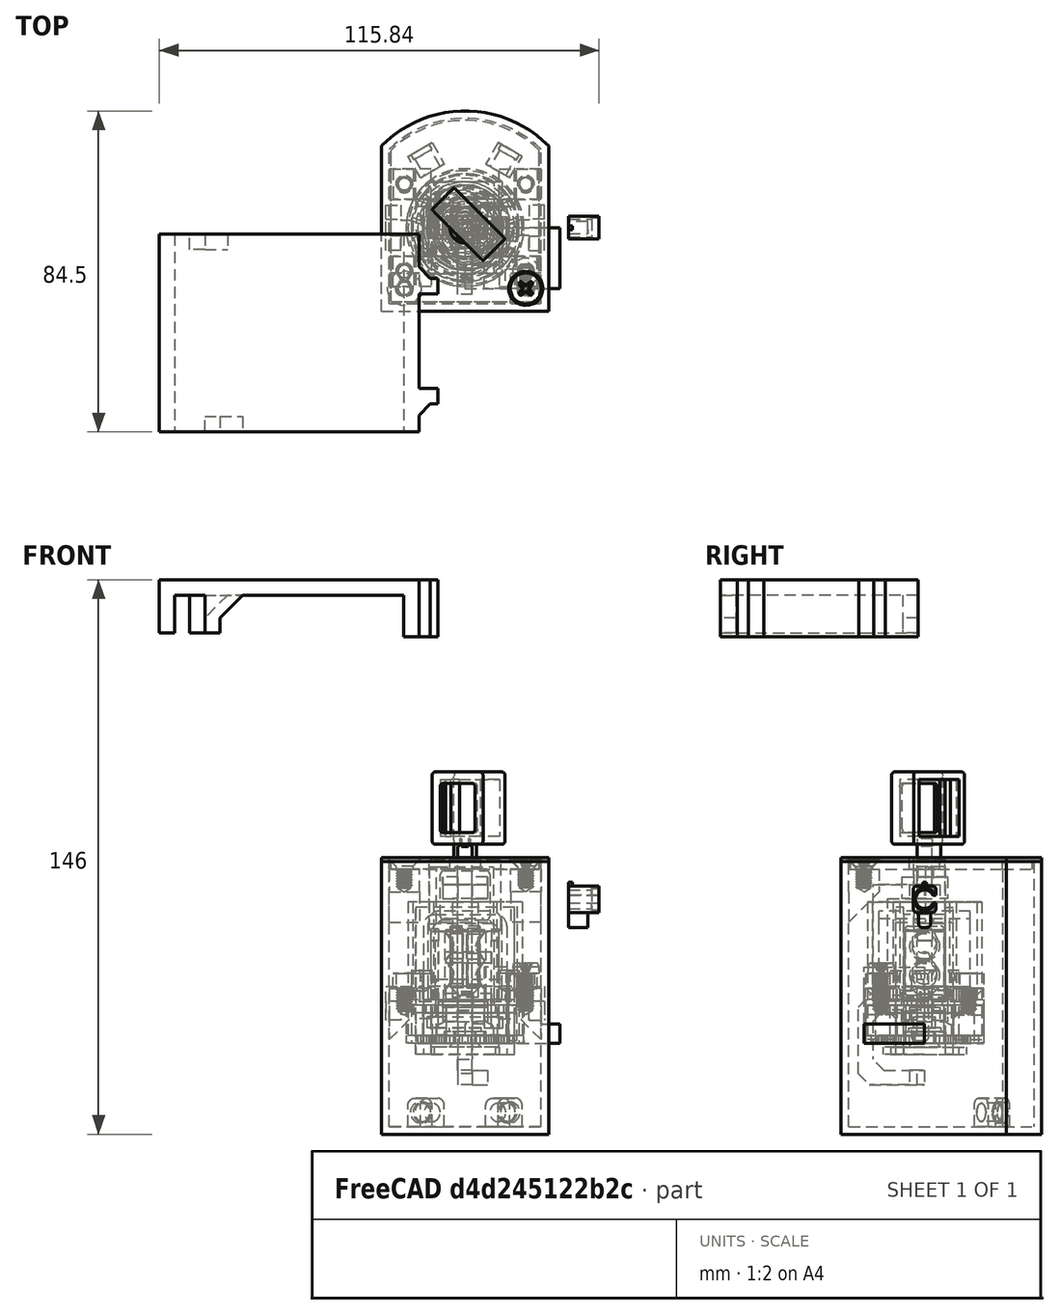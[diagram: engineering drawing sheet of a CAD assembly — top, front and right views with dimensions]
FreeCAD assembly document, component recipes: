
FREECAD ASSEMBLY — COMPONENT RECIPES ("laser2-1mm")

This assembly document has 31 components, labeled P0..P30 below (a component is one placed body or linked part). 31 of them carry a construction recipe — the FreeCAD feature program that regenerates the part from scratch, quoted from this document or its linked companion documents; the rest are supplied as boundary geometry only. No exploded tour is included for this assembly.
NOTE — this tour is split across 2 documents so each fits a 32k-token context. This is document 1: the component sections continue in the remaining 1 document, each repeating the header above.
COMPONENT P0 — recipe-attached ("stator", modeled in this document).
Construction recipe (the document's own serialized feature program — sketch geometry with constraints, then the solid features built on it; lengths are millimeters unless a unit is written):

FEATURE [PartDesign::SubShapeBinder] Binder
  BindCopyOnChange = 0
  BindMode = 0
  ClaimChildren = false
  Context = -> Body [Binder.]
  Fuse = false
  MakeFace = true
  OffsetFill = false
  OffsetIntersection = false
  OffsetJoinType = 0
  OffsetOpenResult = false
  PartialLoad = false
  Refine = true
  Relative = true
  Support = -> [Body020]
  _Version = 2
FEATURE [Sketcher::SketchObject] Sketch100
  ArcFitTolerance = 1e-06
  AttachmentSupport = -> [Origin]
  ExternalGeometry = -> [Binder]
  ExternalTypes = [0,0]
  FullyConstrained = false
  MakeInternals = false
  MapMode = 5
  sketch-geometry (3):
    g0: Circle CenterX=0 CenterY=0 CenterZ=0 NormalX=0 NormalY=0 NormalZ=1 AngleXU=0 Radius=11.2
    g1: GeomPoint [constr] X=-5.17153 Y=14.2087 Z=0
    g2: Circle CenterX=0 CenterY=0 CenterZ=0 NormalX=0 NormalY=0 NormalZ=1 AngleXU=0 Radius=14.2
  constraints (4):
    c: Coincident(g0,g-4)
    c: Distance(g-4,g0) = 0.2
    c: Coincident(g2,g0)
    c: Distance(g2,g0) = 3
FEATURE [PartDesign::Pad] Pad
  Direction = (0,0,1)
  Length = 10
  Length2 = 10
  Profile = -> Sketch100
  ReferenceAxis = -> Sketch100 [N_Axis]
  Refine = true
  SideType = 0
  Suppressed = false
  Type = 3
  Type2 = 0
  UpToFace = -> Binder [Face1]
FEATURE [PartDesign::SubShapeBinder] Binder024
  BindCopyOnChange = 0
  BindMode = 0
  ClaimChildren = false
  Context = -> Body [Binder024.]
  Fuse = false
  MakeFace = true
  OffsetFill = false
  OffsetIntersection = false
  OffsetJoinType = 0
  OffsetOpenResult = false
  PartialLoad = false
  Refine = true
  Relative = true
  Support = -> [Body022]
  _Version = 2
FEATURE [Sketcher::SketchObject] Sketch102
  ArcFitTolerance = 1e-06
  AttachmentSupport = -> [Binder024]
  ExternalGeometry = -> [Binder024]
  ExternalTypes = [0,0]
  FullyConstrained = true
  MakeInternals = false
  MapMode = 5
  Placement = pos=(-7,0,0) rot=(0.57735,0.57735,0.57735;2.0944rad)
  sketch-geometry (2):
    g0: LineSegment [constr] StartX=0 StartY=13 StartZ=0 EndX=0 EndY=21 EndZ=0
    g1: GeomPoint X=0 Y=17 Z=0
  constraints (5):
    c: PointOnObject(g0,g-4)
    c: PointOnObject(g0,g-3)
    c: Vertical(g0)
    c: PointOnObject(g0,g-2)
    c: Symmetric(g0,g0,g1)
FEATURE [Part::DatumPlane] DatumPlane003
  AttachmentSupport = -> [Sketch102]
  MapMode = 1
  Placement = pos=(-7,0,17) rot=(0,0,1;0rad)
FEATURE [Sketcher::SketchObject] Sketch104
  ArcFitTolerance = 1e-06
  AttachmentSupport = -> [Pad]
  ExternalGeometry = -> [Pad]
  ExternalTypes = [0,0]
  FullyConstrained = true
  MakeInternals = false
  MapMode = 5
  Placement = pos=(0,0,2) rot=(0,0,1;0rad)
  expr: Constraints[9] = VarSet.target_angle * 2
  sketch-geometry (6):
    g0: ArcOfCircle CenterX=0 CenterY=0 CenterZ=0 NormalX=0 NormalY=0 NormalZ=1 AngleXU=0 Radius=14.2 StartAngle=0 EndAngle=0.698132
    g1: GeomPoint X=14.2 Y=0 Z=0
    g2: LineSegment StartX=10.8778 StartY=9.12758 StartZ=0 EndX=8.5797 EndY=7.19922 EndZ=0
    g3: LineSegment StartX=14.2 StartY=0 StartZ=0 EndX=11.2 EndY=0 EndZ=0
    g4: ArcOfCircle CenterX=0 CenterY=0 CenterZ=0 NormalX=0 NormalY=0 NormalZ=1 AngleXU=0 Radius=11.2 StartAngle=0 EndAngle=0.698132
    g5: LineSegment [constr] StartX=0 StartY=0 StartZ=0 EndX=10.8778 EndY=9.12758 EndZ=0
  constraints (15):
    c: Coincident(g0,g-1)
    c: PointOnObject(g1,g-1)
    c: Coincident(g0,g1)
    c: Coincident(g3,g0)
    c: PointOnObject(g3,g-1)
    c: Coincident(g3,g4)
    c: Coincident(g4,g2)
    c: Coincident(g4,g-1)
    c: Coincident(g5,g-1)
    c: Angle(g-1,g5) = 0.698132
    c: PointOnObject(g5,g-3)
    c: Coincident(g0,g5)
    c: Coincident(g2,g0)
    c: PointOnObject(g2,g5)
    c: PointOnObject(g2,g-4)
FEATURE [PartDesign::Pad] Pad065
  BaseFeature = -> Pad
  Direction = (0,0,1)
  Length = 10
  Length2 = 10
  Offset = 2.13333
  Profile = -> Sketch104
  ReferenceAxis = -> Sketch104 [N_Axis]
  Refine = true
  SideType = 0
  Suppressed = false
  Type = 3
  Type2 = 0
  UpToFace = -> DatumPlane003
  expr: Offset = 2 / 3 * VarSet.magnet_diameter / 2
FEATURE [Sketcher::SketchObject] Sketch105
  ArcFitTolerance = 1e-06
  AttachmentSupport = -> [Pad065]
  ExternalGeometry = -> [Pad065]
  ExternalTypes = [0]
  FullyConstrained = false
  MakeInternals = false
  MapMode = 5
  Placement = pos=(0,0,19.1333) rot=(0,0,1;0rad)
  sketch-geometry (2):
    g0: LineSegment StartX=0 StartY=0 StartZ=0 EndX=10.4708 EndY=3.97514 EndZ=0
    g1: GeomPoint X=10.4708 Y=3.97514 Z=0
  constraints (3):
    c: Coincident(g0,g-5)
    c: PointOnObject(g0,g-5)
    c: Coincident(g0,g1)
FEATURE [Part::DatumPlane] DatumPlane004
  AttachmentOffset = pos=(0,0,2) rot=(0,0,1;0rad)
  AttachmentSupport = -> [Sketch105]
  MapMode = 7
  Placement = pos=(8.60104,3.26529,19.1333) rot=(0.715712,-0.49384,-0.49384;1.89921rad)
FEATURE [Sketcher::SketchObject] Sketch106
  ArcFitTolerance = 1e-06
  AttachmentSupport = -> [DatumPlane004]
  ExternalGeometry = -> [Binder024]
  ExternalTypes = [0,0]
  FullyConstrained = true
  MakeInternals = false
  MapMode = 5
  Placement = pos=(8.60104,3.26529,19.1333) rot=(0.715712,-0.49384,-0.49384;1.89921rad)
  expr: Constraints[11] = VarSet.magnet_diameter
  sketch-geometry (5):
    g0: LineSegment [constr] StartX=2.48446 StartY=-7.63333 StartZ=0 EndX=2.48446 EndY=-6.13333 EndZ=0
    g1: LineSegment [constr] StartX=2.48446 StartY=-6.13333 StartZ=0 EndX=2.48446 EndY=1.86667 EndZ=0
    g2: GeomPoint [constr] X=2.48446 Y=-2.13333 Z=0
    g3: LineSegment [constr] StartX=2.48446 StartY=-2.13333 StartZ=0 EndX=0 EndY=-2.13333 EndZ=0
    g4: Circle CenterX=0 CenterY=-2.13333 CenterZ=0 NormalX=0 NormalY=0 NormalZ=1 AngleXU=0 Radius=3.2
  constraints (12):
    c: Coincident(g0,g-4)
    c: PointOnObject(g0,g-4)
    c: Vertical(g0)
    c: Coincident(g1,g0)
    c: PointOnObject(g1,g-3)
    c: Vertical(g1)
    c: Symmetric(g1,g1,g2)
    c: Coincident(g3,g2)
    c: PointOnObject(g3,g-2)
    c: Horizontal(g3)
    c: Coincident(g4,g3)
    c: Diameter(g4) = 6.4
FEATURE [PartDesign::Pocket] Pocket024
  BaseFeature = -> Pad065
  Direction = (0.934895,0.354923,-1e-16)
  Length = 5.2
  Length2 = 5
  Profile = -> Sketch106
  ReferenceAxis = -> Sketch106 [N_Axis]
  Refine = true
  SideType = 0
  Suppressed = false
  Type = 0
  Type2 = 0
  expr: Length = 2 mm + VarSet.magnet_height
FEATURE [PartDesign::Mirrored] Mirror
  MirrorPlane = -> XZ_Plane
  Refine = true
  Suppressed = false
  TransformMode = 0
FEATURE [PartDesign::Mirrored] Mirror008
  MirrorPlane = -> YZ_Plane
  Refine = true
  Suppressed = false
  TransformMode = 0
FEATURE [PartDesign::MultiTransform] MultiTransform
  BaseFeature = -> Pocket024
  Originals = -> [Pad065,Pad,Pocket024]
  Refine = true
  Suppressed = false
  TransformMode = 0
  Transformations = -> [Mirror,Mirror008]
FEATURE [PartDesign::Body] Body  label="stator"
  AllowCompound = false
  Group = -> [Sketch100,Binder,Pad,Binder024,Sketch102,DatumPlane003,Sketch104,Pad065,Sketch105,DatumPlane004,Sketch106,Pocket024,MultiTransform,Mirror,Mirror008]
  Origin = -> Origin
  Tip = -> MultiTransform
COMPONENT P1 — recipe-attached ("bearing", modeled in this document).
Construction recipe (the document's own serialized feature program — sketch geometry with constraints, then the solid features built on it; lengths are millimeters unless a unit is written):

FEATURE [Sketcher::SketchObject] Sketch002
  ArcFitTolerance = 1e-06
  AttachmentSupport = -> [Origin004]
  ExternalTypes = [0]
  FullyConstrained = true
  MakeInternals = false
  MapMode = 5
  expr: Constraints[1] = VarSet.bearing_inner_diameter
  expr: Constraints[3] = VarSet.bearing_diameter
  sketch-geometry (2):
    g0: Circle CenterX=0 CenterY=0 CenterZ=0 NormalX=0 NormalY=0 NormalZ=1 AngleXU=0 Radius=5
    g1: Circle CenterX=0 CenterY=0 CenterZ=0 NormalX=0 NormalY=0 NormalZ=1 AngleXU=0 Radius=13
  constraints (4):
    c: Coincident(g0,g-1)
    c: Diameter(g0) = 10
    c: Coincident(g1,g0)
    c: Diameter(g1) = 26
FEATURE [PartDesign::Pad] Pad001
  Direction = (0,0,1)
  Length = 8
  Length2 = 10
  Profile = -> Sketch002
  ReferenceAxis = -> Sketch002 [N_Axis]
  Refine = true
  SideType = 0
  Suppressed = false
  Type = 0
  Type2 = 0
  expr: Length = VarSet.bearing_height
FEATURE [PartDesign::Body] Body002  label="bearing"
  AllowCompound = false
  Group = -> [Sketch002,Pad001]
  Origin = -> Origin004
  Tip = -> Pad001
COMPONENT P2 — recipe-attached ("mirror_holder_adapter", modeled in this document).
Construction recipe (the document's own serialized feature program — sketch geometry with constraints, then the solid features built on it; lengths are millimeters unless a unit is written):

FEATURE [PartDesign::SubShapeBinder] Binder005
  BindCopyOnChange = 0
  BindMode = 0
  ClaimChildren = false
  Context = -> Body004 [Binder005.]
  Fuse = false
  MakeFace = true
  OffsetFill = false
  OffsetIntersection = false
  OffsetJoinType = 0
  OffsetOpenResult = false
  PartialLoad = false
  Refine = true
  Relative = true
  _Version = 2
FEATURE [Sketcher::SketchObject] Sketch028
  ArcFitTolerance = 1e-06
  AttachmentSupport = -> [Binder005]
  ExternalGeometry = -> [Binder005]
  ExternalTypes = [0,0,0,0,0,0,0]
  FullyConstrained = false
  MakeInternals = false
  MapMode = 5
  Placement = pos=(0,0,11) rot=(0,0,1;0rad)
  sketch-geometry (13):
    g0: LineSegment StartX=20.8819 StartY=-6 StartZ=0 EndX=20.8819 EndY=6 EndZ=0
    g1: LineSegment StartX=20.8819 StartY=6 StartZ=0 EndX=16.8819 EndY=6 EndZ=0
    g2: LineSegment StartX=16.8819 StartY=-6 StartZ=0 EndX=20.8819 EndY=-6 EndZ=0
    g3: GeomPoint [constr] X=17 Y=0 Z=0
    g4: LineSegment [constr] StartX=16.8819 StartY=6 StartZ=0 EndX=20.8819 EndY=-6 EndZ=0
    g5: GeomPoint [constr] X=18.8819 Y=0 Z=0
    g6: LineSegment StartX=16.8819 StartY=6 StartZ=0 EndX=16.8819 EndY=2 EndZ=0
    g7: ArcOfCircle CenterX=0 CenterY=0 CenterZ=0 NormalX=0 NormalY=0 NormalZ=1 AngleXU=0 Radius=12 StartAngle=0.167448 EndAngle=6.11574
    g8: LineSegment StartX=16.8819 StartY=2 StartZ=0 EndX=11.8322 EndY=2 EndZ=0
    g9: LineSegment StartX=16.8819 StartY=-2 StartZ=0 EndX=11.8322 EndY=-2 EndZ=0
    g10: LineSegment StartX=16.8819 StartY=-6 StartZ=0 EndX=16.8819 EndY=-2 EndZ=0
    g11: LineSegment StartX=16.8819 StartY=-2 StartZ=0 EndX=16.8819 EndY=-2 EndZ=0
    g12: LineSegment [constr] StartX=16.8819 StartY=2 StartZ=0 EndX=16.8819 EndY=-2 EndZ=0
FEATURE [PartDesign::Pad] Pad019
  Direction = (0,0,1)
  Length = 4
  Length2 = 10
  Profile = -> Sketch028
  ReferenceAxis = -> Sketch028 [N_Axis]
  Refine = true
  SideType = 0
  Suppressed = false
  Type = 0
  Type2 = 0
FEATURE [Sketcher::SketchObject] Sketch029
  ArcFitTolerance = 1e-06
  AttachmentSupport = -> [Pad019]
  ExternalGeometry = -> [Pad019,Binder005]
  ExternalTypes = [0,0,0,0,0,0,0]
  FullyConstrained = true
  MakeInternals = false
  MapMode = 5
  Placement = pos=(0,0,11) rot=(1,0,0;3.14159rad)
  sketch-geometry (8):
    g0: LineSegment StartX=16.8819 StartY=6 StartZ=0 EndX=16.8819 EndY=2.2 EndZ=0
    g1: LineSegment StartX=16.8819 StartY=2.2 StartZ=0 EndX=20.8819 EndY=2.2 EndZ=0
    g2: LineSegment StartX=20.8819 StartY=2.2 StartZ=0 EndX=20.8819 EndY=6 EndZ=0
    g3: LineSegment StartX=20.8819 StartY=6 StartZ=0 EndX=16.8819 EndY=6 EndZ=0
    g4: LineSegment StartX=16.8819 StartY=-6 StartZ=0 EndX=20.8819 EndY=-6 EndZ=0
    g5: LineSegment StartX=20.8819 StartY=-6 StartZ=0 EndX=20.8819 EndY=-2.2 EndZ=0
    g6: LineSegment StartX=20.8819 StartY=-2.2 StartZ=0 EndX=16.8819 EndY=-2.2 EndZ=0
    g7: LineSegment StartX=16.8819 StartY=-2.2 StartZ=0 EndX=16.8819 EndY=-6 EndZ=0
  constraints (22):
    c: PointOnObject(g0,g-5)
    c: PointOnObject(g0,g-5)
    c: Coincident(g1,g0)
    c: PointOnObject(g1,g-3)
    c: Horizontal(g1)
    c: Coincident(g2,g1)
    c: Coincident(g2,g-4)
    c: Coincident(g3,g2)
    c: Coincident(g3,g0)
    c: Horizontal(g3)
    c: Distance(g-8,g1) = 0.2
    c: Coincident(g4,g5)
    c: Coincident(g5,g6)
    c: Coincident(g6,g7)
    c: Coincident(g7,g4)
    c: Horizontal(g4)
    c: Horizontal(g6)
    c: Vertical(g5)
    c: Vertical(g7)
    c: Coincident(g4,g-9)
    c: PointOnObject(g5,g-3)
    c: Distance(g-7,g6) = 0.2
FEATURE [PartDesign::Pad] Pad020
  BaseFeature = -> Pad019
  Direction = (0,0,-1)
  Length = 10
  Length2 = 10
  Profile = -> Sketch029
  ReferenceAxis = -> Sketch029 [N_Axis]
  Refine = true
  SideType = 0
  Suppressed = false
  Type = 3
  Type2 = 0
  UpToFace = -> Binder005 [Face13]
FEATURE [PartDesign::Mirrored] Mirror004
  MirrorPlane = -> Sketch029 [V_Axis]
  Refine = true
  Suppressed = false
  TransformMode = 0
FEATURE [PartDesign::MultiTransform] MultiTransform002
  BaseFeature = -> Pad020
  Originals = -> [Pad020,Pad019]
  Refine = true
  Suppressed = false
  TransformMode = 0
  Transformations = -> [Mirror004]
FEATURE [Sketcher::SketchObject] Sketch030
  ArcFitTolerance = 1e-06
  AttachmentSupport = -> [MultiTransform002]
  ExternalTypes = [0]
  FullyConstrained = true
  MakeInternals = false
  MapMode = 5
  Placement = pos=(0,0,15) rot=(0,0,1;0rad)
  sketch-geometry (12):
    g0: LineSegment StartX=-0.707107 StartY=5.29289 StartZ=0 EndX=-5.29289 EndY=0.707107 EndZ=0
    g1: LineSegment StartX=-5.29289 StartY=-0.707107 StartZ=0 EndX=-0.707107 EndY=-5.29289 EndZ=0
    g2: LineSegment StartX=0.707107 StartY=-5.29289 StartZ=0 EndX=5.29289 EndY=-0.707107 EndZ=0
    g3: LineSegment StartX=5.29289 StartY=0.707107 StartZ=0 EndX=0.707107 EndY=5.29289 EndZ=0
    g4: ArcOfCircle CenterX=-3e-16 CenterY=4.58579 CenterZ=0 NormalX=0 NormalY=0 NormalZ=1 AngleXU=0 Radius=1 StartAngle=0.785398 EndAngle=2.35619
    g5: GeomPoint [constr] X=0 Y=6 Z=0
    g6: ArcOfCircle CenterX=-4.58579 CenterY=6e-16 CenterZ=0 NormalX=0 NormalY=0 NormalZ=1 AngleXU=0 Radius=1 StartAngle=2.35619 EndAngle=3.92699
    g7: GeomPoint [constr] X=-6 Y=0 Z=0
    g8: ArcOfCircle CenterX=-3e-16 CenterY=-4.58579 CenterZ=0 NormalX=0 NormalY=0 NormalZ=1 AngleXU=0 Radius=1 StartAngle=3.92699 EndAngle=5.49779
    g9: GeomPoint [constr] X=0 Y=-6 Z=0
    g10: ArcOfCircle CenterX=4.58579 CenterY=-3e-16 CenterZ=0 NormalX=0 NormalY=0 NormalZ=1 AngleXU=0 Radius=1 StartAngle=5.49779 EndAngle=7.06858
    g11: GeomPoint [constr] X=6 Y=0 Z=0
  constraints (26):
    c: PointOnObject(g5,g-2)
    c: PointOnObject(g7,g-1)
    c: Symmetric(g9,g5,g-1)
    c: Symmetric(g7,g11,g-1)
    c: Distance(g-1,g11) = 6
    c: Distance(g9,g-1) = 6
    c: PointOnObject(g5,g0)
    c: PointOnObject(g5,g3)
    c: Tangent(g0,g4) = -1.5708
    c: Tangent(g3,g4) = -1.5708
    c: PointOnObject(g7,g0)
    c: PointOnObject(g7,g1)
    c: Tangent(g0,g6) = -1.5708
    c: Tangent(g1,g6) = -1.5708
    c: PointOnObject(g9,g1)
    c: PointOnObject(g9,g2)
    c: Tangent(g1,g8) = -1.5708
    c: Tangent(g2,g8) = -1.5708
    c: PointOnObject(g11,g2)
    c: PointOnObject(g11,g3)
    c: Tangent(g2,g10) = -1.5708
    c: Tangent(g3,g10) = -1.5708
    c: Distance(g10,g2) = 1
    c: Distance(g1,g6) = 1
    c: Distance(g1,g8) = 1
    c: Distance(g4,g3) = 1
FEATURE [PartDesign::Pocket] Pocket
  BaseFeature = -> MultiTransform002
  Direction = (0,0,-1)
  Length = 5
  Length2 = 5
  Profile = -> Sketch030
  ReferenceAxis = -> Sketch030 [N_Axis]
  Refine = true
  SideType = 0
  Suppressed = false
  Type = 2
  Type2 = 0
FEATURE [Sketcher::SketchObject] Sketch070
  ArcFitTolerance = 1e-06
  AttachmentSupport = -> [Pocket]
  ExternalGeometry = -> [Pocket]
  ExternalTypes = [0,0,0,0,0,0,0,0]
  FullyConstrained = true
  MakeInternals = false
  MapMode = 5
  Placement = pos=(0,0,15) rot=(0,0,1;0rad)
  sketch-geometry (20):
    g0: ArcOfCircle CenterX=-4.58579 CenterY=7e-16 CenterZ=0 NormalX=0 NormalY=0 NormalZ=1 AngleXU=0 Radius=2 StartAngle=2.35619 EndAngle=3.92699
    g1: LineSegment StartX=-6 StartY=-1.41421 StartZ=0 EndX=-1.41421 EndY=-6 EndZ=0
    g2: ArcOfCircle CenterX=-6e-16 CenterY=-4.58579 CenterZ=0 NormalX=0 NormalY=0 NormalZ=1 AngleXU=0 Radius=2 StartAngle=3.92699 EndAngle=5.49779
    g3: LineSegment StartX=1.41421 StartY=-6 StartZ=0 EndX=6 EndY=-1.41421 EndZ=0
    g4: ArcOfCircle CenterX=4.58579 CenterY=0 CenterZ=0 NormalX=0 NormalY=0 NormalZ=1 AngleXU=0 Radius=2 StartAngle=5.49779 EndAngle=7.06858
    g5: LineSegment StartX=6 StartY=1.41421 StartZ=0 EndX=1.41421 EndY=6 EndZ=0
    g6: ArcOfCircle CenterX=-2.1e-15 CenterY=4.58579 CenterZ=0 NormalX=0 NormalY=0 NormalZ=1 AngleXU=0 Radius=2 StartAngle=0.785398 EndAngle=2.35619
    g7: LineSegment StartX=-1.41421 StartY=6 StartZ=0 EndX=-6 EndY=1.41421 EndZ=0
    g8: LineSegment [constr] StartX=-0.707107 StartY=5.29289 StartZ=0 EndX=-2.1e-15 EndY=4.58579 EndZ=0
    g9: LineSegment [constr] StartX=-2.1e-15 StartY=4.58579 StartZ=0 EndX=0.707107 EndY=5.29289 EndZ=0
    g10: LineSegment [constr] StartX=5.29289 StartY=0.707107 StartZ=0 EndX=4.58579 EndY=0 EndZ=0
    g11: LineSegment [constr] StartX=5.29289 StartY=-0.707107 StartZ=0 EndX=4.58579 EndY=0 EndZ=0
    g12: LineSegment [constr] StartX=0.707107 StartY=-5.29289 StartZ=0 EndX=-6e-16 EndY=-4.58579 EndZ=0
    g13: LineSegment [constr] StartX=-6e-16 StartY=-4.58579 StartZ=0 EndX=-0.707107 EndY=-5.29289 EndZ=0
    g14: LineSegment [constr] StartX=-5.29289 StartY=-0.707107 StartZ=0 EndX=-4.58579 EndY=7e-16 EndZ=0
    g15: LineSegment [constr] StartX=-4.58579 StartY=7e-16 StartZ=0 EndX=-5.29289 EndY=0.707107 EndZ=0
    g16: LineSegment [constr] StartX=5.29289 StartY=0.707107 StartZ=0 EndX=6 EndY=1.41421 EndZ=0
    g17: LineSegment [constr] StartX=5.29289 StartY=-0.707107 StartZ=0 EndX=6 EndY=-1.41421 EndZ=0
    g18: LineSegment [constr] StartX=0.707107 StartY=5.29289 StartZ=0 EndX=1.41421 EndY=6 EndZ=0
    g19: LineSegment [constr] StartX=-0.707107 StartY=5.29289 StartZ=0 EndX=-1.41421 EndY=6 EndZ=0
  constraints (45):
    c: Tangent(g0,g1) = -1.5708
    c: Tangent(g0,g7) = -1.5708
    c: Tangent(g1,g2) = -1.5708
    c: Tangent(g2,g3) = -1.5708
    c: Tangent(g3,g4) = -1.5708
    c: Tangent(g4,g5) = -1.5708
    c: Tangent(g5,g6) = -1.5708
    c: Tangent(g6,g7) = -1.5708
    c: Distance(g-10,g0) = 1
    c: Distance(g0,g-10) = 1
    c: Distance(g-7,g3) = 1
    c: Distance(g-6,g4) = 1
    c: Coincident(g8,g-4)
    c: Coincident(g8,g6)
    c: Coincident(g9,g6)
    c: PointOnObject(g9,g-4)
    c: Coincident(g10,g-6)
    c: Coincident(g10,g4)
    c: Coincident(g11,g-7)
    c: Coincident(g11,g4)
    c: Coincident(g12,g-8)
    c: Coincident(g12,g2)
    c: Coincident(g13,g2)
    c: Coincident(g13,g-9)
    c: Coincident(g14,g-10)
    c: Coincident(g14,g0)
    c: Coincident(g15,g0)
    c: Coincident(g15,g-10)
    c: Equal(g8,g9)
    c: Equal(g9,g10)
    c: Equal(g10,g11)
    c: Equal(g11,g12)
    c: Equal(g12,g13)
    c: Equal(g13,g14)
    c: Coincident(g16,g10)
    c: Coincident(g16,g4)
    c: Coincident(g17,g11)
    c: Coincident(g17,g3)
    c: Parallel(g17,g11)
    c: Coincident(g18,g9)
    c: Coincident(g18,g5)
    c: Coincident(g19,g8)
    c: Coincident(g19,g6)
    c: Parallel(g19,g8)
    c: Parallel(g18,g9)
FEATURE [PartDesign::Pad] Pad045
  BaseFeature = -> Pocket
  Direction = (0,0,1)
  Length = 7
  Length2 = 10
  Profile = -> Sketch070
  ReferenceAxis = -> Sketch070 [N_Axis]
  Refine = true
  SideType = 0
  Suppressed = false
  Type = 0
  Type2 = 0
FEATURE [PartDesign::Body] Body004  label="mirror_holder_adapter"
  AllowCompound = false
  Group = -> [Binder005,Sketch028,Pad019,Sketch029,Pad020,MultiTransform002,Mirror004,Sketch030,Pocket,Sketch070,Pad045]
  Origin = -> Origin009
  Tip = -> Pocket
COMPONENT P3 — recipe-attached ("mirror_base", modeled in this document).
Construction recipe (the document's own serialized feature program — sketch geometry with constraints, then the solid features built on it; lengths are millimeters unless a unit is written):

FEATURE [PartDesign::SubShapeBinder] Binder006
  BindCopyOnChange = 0
  BindMode = 0
  ClaimChildren = false
  Context = -> Body005 [Binder006.]
  Fuse = false
  MakeFace = true
  OffsetFill = false
  OffsetIntersection = false
  OffsetJoinType = 0
  OffsetOpenResult = false
  PartialLoad = false
  Refine = true
  Relative = true
  Support = -> [Body004]
  _Version = 2
FEATURE [Sketcher::SketchObject] Sketch031
  ArcFitTolerance = 1e-06
  AttachmentSupport = -> [Binder006]
  ExternalGeometry = -> [Binder006]
  ExternalTypes = [0,0,0,0,0,0,0,0]
  FullyConstrained = true
  MakeInternals = false
  MapMode = 5
  Placement = pos=(0,0,11) rot=(1,0,0;3.14159rad)
  sketch-geometry (16):
    g0: ArcOfCircle CenterX=-4.58579 CenterY=9e-16 CenterZ=0 NormalX=0 NormalY=0 NormalZ=1 AngleXU=-1.5708 Radius=0.85 StartAngle=3.92699 EndAngle=5.49779
    g1: LineSegment StartX=-5.18683 StartY=-0.601041 StartZ=0 EndX=-0.601041 EndY=-5.18683 EndZ=0
    g2: ArcOfCircle CenterX=-9e-16 CenterY=-4.58579 CenterZ=0 NormalX=0 NormalY=0 NormalZ=1 AngleXU=-1.5708 Radius=0.85 StartAngle=5.49779 EndAngle=7.06858
    g3: LineSegment StartX=0.601041 StartY=-5.18683 StartZ=0 EndX=5.18683 EndY=-0.601041 EndZ=0
    g4: ArcOfCircle CenterX=4.58579 CenterY=-9e-16 CenterZ=0 NormalX=0 NormalY=0 NormalZ=1 AngleXU=-1.5708 Radius=0.85 StartAngle=0.785398 EndAngle=2.35619
    g5: LineSegment StartX=5.18683 StartY=0.601041 StartZ=0 EndX=0.601041 EndY=5.18683 EndZ=0
    g6: ArcOfCircle CenterX=0 CenterY=4.58579 CenterZ=0 NormalX=0 NormalY=0 NormalZ=1 AngleXU=-1.5708 Radius=0.85 StartAngle=2.35619 EndAngle=3.92699
    g7: LineSegment StartX=-0.601041 StartY=5.18683 StartZ=0 EndX=-5.18683 EndY=0.601041 EndZ=0
    g8: LineSegment [constr] StartX=5.18683 StartY=0.601041 StartZ=0 EndX=4.58579 EndY=-7e-16 EndZ=0
    g9: LineSegment [constr] StartX=4.58579 StartY=-7e-16 StartZ=0 EndX=5.18683 EndY=-0.601041 EndZ=0
    g10: LineSegment [constr] StartX=0.601041 StartY=5.18683 StartZ=0 EndX=3e-16 EndY=4.58579 EndZ=0
    g11: LineSegment [constr] StartX=3e-16 StartY=4.58579 StartZ=0 EndX=-0.601041 EndY=5.18683 EndZ=0
    g12: LineSegment [constr] StartX=-5.18683 StartY=0.601041 StartZ=0 EndX=-4.58579 EndY=1.3e-15 EndZ=0
    g13: LineSegment [constr] StartX=-4.58579 StartY=1.3e-15 StartZ=0 EndX=-5.18683 EndY=-0.601041 EndZ=0
    g14: LineSegment [constr] StartX=-0.601041 StartY=-5.18683 StartZ=0 EndX=-1.1e-15 EndY=-4.58579 EndZ=0
    g15: LineSegment [constr] StartX=-1.2e-15 StartY=-4.58579 StartZ=0 EndX=0.601041 EndY=-5.18683 EndZ=0
  constraints (33):
    c: Tangent(g0,g1) = -1.5708
    c: Tangent(g0,g7) = -1.5708
    c: Tangent(g1,g2) = -1.5708
    c: Tangent(g2,g3) = -1.5708
    c: Tangent(g3,g4) = -1.5708
    c: Tangent(g4,g5) = -1.5708
    c: Tangent(g5,g6) = -1.5708
    c: Tangent(g6,g7) = -1.5708
    c: Coincident(g8,g4)
    c: Coincident(g8,g4)
    c: Coincident(g9,g4)
    c: Coincident(g9,g3)
    c: Perpendicular(g8,g9)
    c: Coincident(g10,g5)
    c: Coincident(g10,g6)
    c: Coincident(g11,g6)
    c: Coincident(g11,g6)
    c: Distance(g11,g11) = 0.85
    c: Perpendicular(g10,g11)
    c: Coincident(g12,g0)
    c: Coincident(g12,g0)
    c: Coincident(g13,g0)
    c: Coincident(g13,g0)
    c: Perpendicular(g12,g13)
    c: Distance(g12,g12) = 0.85
    c: Coincident(g14,g1)
    c: Coincident(g14,g2)
    c: Coincident(g15,g2)
    c: Coincident(g15,g2)
    c: Distance(g15,g15) = 0.85
    c: Coincident(g0,g-10)
    c: Coincident(g6,g-5)
    c: Coincident(g4,g-6)
FEATURE [PartDesign::Pad] Pad021
  Direction = (0,0,-1)
  Length = 18.4
  Length2 = 10
  Offset = 16
  Profile = -> Sketch031
  ReferenceAxis = -> Sketch031 [N_Axis]
  Refine = true
  Reversed = true
  SideType = 0
  Suppressed = false
  Type = 0
  Type2 = 0
FEATURE [PartDesign::Body] Body005  label="mirror_base"
  AllowCompound = false
  Group = -> [Sketch031,Binder006,Pad021]
  Origin = -> Origin011
  Placement = pos=(0,0,0) rot=(0,0,1;-1.5708rad)
  Tip = -> Pad021
COMPONENT P4 — recipe-attached ("cover", modeled in this document).
Construction recipe (the document's own serialized feature program — sketch geometry with constraints, then the solid features built on it; lengths are millimeters unless a unit is written):

FEATURE [PartDesign::SubShapeBinder] Binder011
  BindCopyOnChange = 0
  BindMode = 0
  ClaimChildren = false
  Context = -> Body006 [Binder011.]
  Fuse = false
  MakeFace = true
  OffsetFill = false
  OffsetIntersection = false
  OffsetJoinType = 0
  OffsetOpenResult = false
  PartialLoad = false
  Refine = true
  Relative = true
  Support = -> [Body008]
  _Version = 2
FEATURE [Sketcher::SketchObject] Sketch036
  ArcFitTolerance = 1e-06
  AttachmentSupport = -> [Binder011]
  ExternalGeometry = -> [Binder011]
  ExternalTypes = [0,0,0,0]
  FullyConstrained = true
  MakeInternals = false
  MapMode = 5
  Placement = pos=(-7.5,0,0) rot=(0.57735,0.57735,0.57735;2.0944rad)
  sketch-geometry (6):
    g0: LineSegment StartX=-1.98579 StartY=16.8 StartZ=0 EndX=-1.98579 EndY=2.2 EndZ=0
    g1: LineSegment StartX=-1.98579 StartY=2.2 StartZ=0 EndX=-0.385786 EndY=2.2 EndZ=0
    g2: LineSegment StartX=-0.385786 StartY=2.2 StartZ=0 EndX=-0.385786 EndY=16.8 EndZ=0
    g3: LineSegment StartX=-0.385786 StartY=16.8 StartZ=0 EndX=-1.98579 EndY=16.8 EndZ=0
    g4: LineSegment [constr] StartX=-0.185786 StartY=2 StartZ=0 EndX=-2.18579 EndY=17 EndZ=0
    g5: GeomPoint [constr] X=-1.18579 Y=9.5 Z=0
  constraints (14):
    c: Coincident(g0,g1)
    c: Coincident(g1,g2)
    c: Coincident(g2,g3)
    c: Coincident(g3,g0)
    c: Vertical(g0)
    c: Vertical(g2)
    c: Horizontal(g1)
    c: Horizontal(g3)
    c: Coincident(g4,g-6)
    c: Coincident(g4,g-4)
    c: Symmetric(g4,g4,g5)
    c: Symmetric(g2,g0,g5)
    c: Distance(g-3,g3) = 0.2
    c: Distance(g-5,g2) = 0.2
FEATURE [PartDesign::Pad] Pad024
  Direction = (1,0,0)
  Length = 10
  Length2 = 10
  Offset = -2
  Profile = -> Sketch036
  ReferenceAxis = -> Sketch036 [N_Axis]
  Refine = true
  SideType = 0
  Suppressed = false
  Type = 3
  Type2 = 0
  UpToFace = -> Binder011 [Face6]
FEATURE [Sketcher::SketchObject] Sketch037
  ArcFitTolerance = 1e-06
  AttachmentSupport = -> [Pad024]
  ExternalGeometry = -> [Pad024]
  ExternalTypes = [0]
  FullyConstrained = true
  MakeInternals = false
  MapMode = 5
  Placement = pos=(11.5,0,0) rot=(0.57735,0.57735,0.57735;2.0944rad)
  sketch-geometry (6):
    g0: LineSegment StartX=-3.48579 StartY=18.3 StartZ=0 EndX=-3.48579 EndY=0.7 EndZ=0
    g1: LineSegment StartX=-3.48579 StartY=0.7 StartZ=0 EndX=1.11421 EndY=0.7 EndZ=0
    g2: LineSegment StartX=1.11421 StartY=0.7 StartZ=0 EndX=1.11421 EndY=18.3 EndZ=0
    g3: LineSegment StartX=1.11421 StartY=18.3 StartZ=0 EndX=-3.48579 EndY=18.3 EndZ=0
    g4: LineSegment [constr] StartX=-1.98579 StartY=16.8 StartZ=0 EndX=-0.385786 EndY=2.2 EndZ=0
    g5: GeomPoint [constr] X=-1.18579 Y=9.5 Z=0
  constraints (14):
    c: Coincident(g0,g1)
    c: Coincident(g1,g2)
    c: Coincident(g2,g3)
    c: Coincident(g3,g0)
    c: Vertical(g0)
    c: Vertical(g2)
    c: Horizontal(g1)
    c: Horizontal(g3)
    c: Coincident(g4,g-6)
    c: Coincident(g4,g-4)
    c: Symmetric(g4,g4,g5)
    c: Symmetric(g0,g2,g5)
    c: Distance(g3,g-5) = 1.5
    c: Distance(g2,g-4) = 1.5
FEATURE [PartDesign::Pad] Pad025
  BaseFeature = -> Pad024
  Direction = (1,0,0)
  Length = 2
  Length2 = 10
  Profile = -> Sketch037
  ReferenceAxis = -> Sketch037 [N_Axis]
  Refine = true
  SideType = 0
  Suppressed = false
  Type = 0
  Type2 = 0
FEATURE [PartDesign::Fillet] Fillet003
  Base = -> Pad025 [Edge17,Edge20,Edge18,Edge22]
  BaseFeature = -> Pad025
  Radius = 1
  Refine = true
  SupportTransform = false
  Suppressed = false
  UseAllEdges = false
FEATURE [PartDesign::Body] Body006  label="cover"
  AllowCompound = false
  Group = -> [Binder011,Sketch036,Pad024,Sketch037,Pad025,Fillet003]
  Origin = -> Origin013
  Tip = -> Fillet003
COMPONENT P5 — recipe-attached ("mirror", modeled in this document).
Construction recipe (the document's own serialized feature program — sketch geometry with constraints, then the solid features built on it; lengths are millimeters unless a unit is written):

FEATURE [Sketcher::SketchObject] Sketch044
  ArcFitTolerance = 1e-06
  AttachmentSupport = -> [Origin019]
  ExternalTypes = [0]
  FullyConstrained = true
  MakeInternals = false
  MapMode = 5
  expr: Constraints[14] = 1 mm + 1.8 mm
  expr: Constraints[8] = VarSet.mirror_width + 2 * 2 mm
  sketch-geometry (7):
    g0: LineSegment StartX=-9.5 StartY=2.8 StartZ=0 EndX=-9.5 EndY=-5.38579 EndZ=0
    g1: LineSegment StartX=-9.5 StartY=-5.38579 StartZ=0 EndX=9.5 EndY=-5.38579 EndZ=0
    g2: LineSegment StartX=9.5 StartY=-5.38579 StartZ=0 EndX=9.5 EndY=2.8 EndZ=0
    g3: LineSegment StartX=9.5 StartY=2.8 StartZ=0 EndX=-9.5 EndY=2.8 EndZ=0
    g4: LineSegment [constr] StartX=-9.5 StartY=-5.38579 StartZ=0 EndX=0 EndY=0 EndZ=0
    g5: LineSegment [constr] StartX=0 StartY=0 StartZ=0 EndX=9.5 EndY=-5.38579 EndZ=0
    g6: GeomPoint [constr] X=0 Y=-5.38579 Z=0
  constraints (18):
    c: Coincident(g0,g1)
    c: Coincident(g1,g2)
    c: Coincident(g2,g3)
    c: Coincident(g3,g0)
    c: Vertical(g0)
    c: Vertical(g2)
    c: Horizontal(g1)
    c: Horizontal(g3)
    c: Distance(g3,g3) = 19
    c: Coincident(g4,g0)
    c: Coincident(g4,g-1)
    c: Coincident(g5,g4)
    c: Coincident(g5,g1)
    c: Equal(g5,g4)
    c: Distance(g4,g3) = 2.8
    c: PointOnObject(g6,g-3)
    c: PointOnObject(g6,g1)
    c: PointOnObject(g6,g-2)
FEATURE [PartDesign::Pad] Pad031
  Direction = (0,0,1)
  Length = 19
  Length2 = 10
  Profile = -> Sketch044
  ReferenceAxis = -> Sketch044 [N_Axis]
  Refine = true
  SideType = 0
  Suppressed = false
  Type = 0
  Type2 = 0
  expr: Length = 2 * 2 mm + VarSet.mirror_width
FEATURE [Sketcher::SketchObject] Sketch045
  ArcFitTolerance = 1e-06
  AttachmentSupport = -> [Pad031]
  ExternalGeometry = -> [Pad031]
  ExternalTypes = [0,0,0,0]
  FullyConstrained = true
  MakeInternals = false
  MapMode = 5
  Placement = pos=(0,-5.38579,0) rot=(1,0,0;1.5708rad)
  sketch-geometry (10):
    g0: LineSegment StartX=-7.5 StartY=17 StartZ=0 EndX=-7.5 EndY=2 EndZ=0
    g1: LineSegment StartX=-7.5 StartY=2 StartZ=0 EndX=7.5 EndY=2 EndZ=0
    g2: LineSegment StartX=7.5 StartY=2 StartZ=0 EndX=7.5 EndY=17 EndZ=0
    g3: LineSegment StartX=7.5 StartY=17 StartZ=0 EndX=-7.5 EndY=17 EndZ=0
    g4: LineSegment StartX=-6.5 StartY=16 StartZ=0 EndX=-6.5 EndY=3 EndZ=0
    g5: LineSegment StartX=-6.5 StartY=3 StartZ=0 EndX=6.5 EndY=3 EndZ=0
    g6: LineSegment StartX=6.5 StartY=3 StartZ=0 EndX=6.5 EndY=16 EndZ=0
    g7: LineSegment StartX=6.5 StartY=16 StartZ=0 EndX=-6.5 EndY=16 EndZ=0
    g8: LineSegment [constr] StartX=9.5 StartY=0 StartZ=0 EndX=-9.5 EndY=19 EndZ=0
    g9: GeomPoint [constr] X=2.45925e-11 Y=9.5 Z=0
  constraints (25):
    c: Coincident(g0,g1)
    c: Coincident(g1,g2)
    c: Coincident(g2,g3)
    c: Coincident(g3,g0)
    c: Vertical(g0)
    c: Vertical(g2)
    c: Horizontal(g1)
    c: Horizontal(g3)
    c: Coincident(g4,g5)
    c: Coincident(g5,g6)
    c: Coincident(g6,g7)
    c: Coincident(g7,g4)
    c: Vertical(g4)
    c: Vertical(g6)
    c: Horizontal(g5)
    c: Horizontal(g7)
    c: Coincident(g8,g-6)
    c: Coincident(g8,g-4)
    c: Symmetric(g8,g8,g9)
    c: Symmetric(g0,g1,g9)
    c: Symmetric(g4,g6,g9)
    c: Distance(g4,g0) = 1
    c: Distance(g-4,g0) = 2
    c: PointOnObject(g0,g8)
    c: PointOnObject(g4,g8)
FEATURE [PartDesign::Pocket] Pocket007
  BaseFeature = -> Pad031
  Direction = (0,1,-2e-16)
  Length = 7.2
  Length2 = 5
  Profile = -> Sketch045 [Edge1,Edge4,Edge3,Edge2]
  ReferenceAxis = -> Sketch045 [N_Axis]
  Refine = true
  SideType = 0
  Suppressed = false
  Type = 0
  Type2 = 0
  expr: Length = 5 mm + 2.2 mm
FEATURE [PartDesign::Pocket] Pocket008
  BaseFeature = -> Pocket007
  Direction = (0,1,-2e-16)
  Length = 5
  Length2 = 5
  Profile = -> Sketch045 [Edge5,Edge8,Edge7,Edge6]
  ReferenceAxis = -> Sketch045 [N_Axis]
  Refine = true
  SideType = 0
  Suppressed = false
  Type = 1
  Type2 = 0
FEATURE [Sketcher::SketchObject] Sketch046
  ArcFitTolerance = 1e-06
  AttachmentSupport = -> [Pocket008]
  ExternalGeometry = -> [Pocket008]
  ExternalTypes = [0]
  FullyConstrained = true
  MakeInternals = false
  MapMode = 5
  Placement = pos=(9.5,0,0) rot=(0.57735,0.57735,0.57735;2.0944rad)
  sketch-geometry (6):
    g0: LineSegment StartX=-0.185786 StartY=17 StartZ=0 EndX=-2.18579 EndY=17 EndZ=0
    g1: LineSegment StartX=-2.18579 StartY=17 StartZ=0 EndX=-2.18579 EndY=2 EndZ=0
    g2: LineSegment StartX=-2.18579 StartY=2 StartZ=0 EndX=-0.185786 EndY=2 EndZ=0
    g3: LineSegment StartX=-0.185786 StartY=17 StartZ=0 EndX=-0.185786 EndY=2 EndZ=0
    g4: LineSegment [constr] StartX=-0.185786 StartY=17 StartZ=0 EndX=1.81421 EndY=17 EndZ=0
    g5: LineSegment [constr] StartX=-0.185786 StartY=2 StartZ=0 EndX=1.81421 EndY=2 EndZ=0
  constraints (16):
    c: Coincident(g0,g1)
    c: Coincident(g1,g2)
    c: Horizontal(g0)
    c: Horizontal(g2)
    c: Vertical(g1)
    c: Distance(g2,g2) = 2
    c: Coincident(g3,g0)
    c: Coincident(g3,g2)
    c: Vertical(g3)
    c: Coincident(g4,g0)
    c: Coincident(g5,g2)
    c: Horizontal(g5)
    c: Horizontal(g4)
    c: Distance(g5,g5) = 2
    c: Coincident(g5,g-3)
    c: Coincident(g4,g-3)
FEATURE [PartDesign::Pocket] Pocket009
  BaseFeature = -> Pocket008
  Direction = (-1,0,0)
  Length = 5
  Length2 = 5
  Profile = -> Sketch046
  ReferenceAxis = -> Sketch046 [N_Axis]
  Refine = true
  SideType = 0
  Suppressed = false
  Type = 2
  Type2 = 0
FEATURE [PartDesign::Fillet] Fillet006
  Base = -> Pocket009 [Edge4,Edge20,Edge19,Edge3,Edge26,Edge27,Edge31,Edge29]
  BaseFeature = -> Pocket009
  Radius = 1
  Refine = true
  SupportTransform = false
  Suppressed = false
  UseAllEdges = false
FEATURE [PartDesign::Body] Body008  label="mirror"
  AllowCompound = false
  Group = -> [Sketch044,Sketch045,Sketch046,Pad031,Pocket007,Pocket008,Pocket009,Fillet006]
  Origin = -> Origin019
  Tip = -> Fillet006
COMPONENT P6 — recipe-attached ("rgb_holder", modeled in this document).
Construction recipe (the document's own serialized feature program — sketch geometry with constraints, then the solid features built on it; lengths are millimeters unless a unit is written):

FEATURE [PartDesign::SubShapeBinder] Binder015
  BindCopyOnChange = 0
  BindMode = 0
  ClaimChildren = false
  Context = -> Body010 [Binder015.]
  Fuse = false
  MakeFace = true
  OffsetFill = false
  OffsetIntersection = false
  OffsetJoinType = 0
  OffsetOpenResult = false
  PartialLoad = false
  Refine = true
  Relative = true
  _Version = 2
FEATURE [Sketcher::SketchObject] Sketch051
  ArcFitTolerance = 1e-06
  AttachmentSupport = -> [Binder015]
  ExternalGeometry = -> [Binder015]
  ExternalTypes = [0,0,0,0]
  FullyConstrained = true
  MakeInternals = false
  MapMode = 5
  Placement = pos=(0,0,30.4) rot=(1,0,0;3.14159rad)
  sketch-geometry (5):
    g0: LineSegment StartX=27.3142 StartY=-1.56045 StartZ=0 EndX=27.3142 EndY=1.56045 EndZ=0
    g1: LineSegment StartX=27.3142 StartY=1.56045 StartZ=0 EndX=32.3142 EndY=1.56045 EndZ=0
    g2: LineSegment StartX=32.3142 StartY=-1.56045 StartZ=0 EndX=27.3142 EndY=-1.56045 EndZ=0
    g3: LineSegment [constr] StartX=27.3142 StartY=-1.56045 StartZ=0 EndX=32.3142 EndY=1.56045 EndZ=0
    g4: LineSegment StartX=32.3142 StartY=1.56045 StartZ=0 EndX=32.3142 EndY=-1.56045 EndZ=0
  constraints (11):
    c: Coincident(g0,g1)
    c: Coincident(g2,g0)
    c: Horizontal(g1)
    c: Coincident(g3,g-4)
    c: Coincident(g3,g-6)
    c: Coincident(g4,g1)
    c: Coincident(g4,g2)
    c: Vertical(g4)
    c: Coincident(g0,g-6)
    c: Coincident(g0,g3)
    c: Coincident(g2,g-5)
FEATURE [PartDesign::Pad] Pad036
  Direction = (0,0,-1)
  Length = 10
  Length2 = 10
  Profile = -> Sketch051
  ReferenceAxis = -> Sketch051 [N_Axis]
  Refine = true
  SideType = 0
  Suppressed = false
  Type = 3
  Type2 = 0
  UpToFace = -> Binder015 [Face15]
FEATURE [Sketcher::SketchObject] Sketch052
  ArcFitTolerance = 1e-06
  AttachmentSupport = -> [Pad036]
  ExternalGeometry = -> [Pad036]
  ExternalTypes = [0,0]
  FullyConstrained = true
  MakeInternals = false
  MapMode = 5
  Placement = pos=(-1.03e-14,0,34.4) rot=(0,0,1;0rad)
  sketch-geometry (6):
    g0: LineSegment StartX=27.3142 StartY=3 StartZ=0 EndX=27.3142 EndY=-3 EndZ=0
    g1: LineSegment StartX=27.3142 StartY=-3 StartZ=0 EndX=35.3142 EndY=-3 EndZ=0
    g2: LineSegment StartX=35.3142 StartY=-3 StartZ=0 EndX=35.3142 EndY=3 EndZ=0
    g3: LineSegment StartX=35.3142 StartY=3 StartZ=0 EndX=27.3142 EndY=3 EndZ=0
    g4: LineSegment [constr] StartX=27.3142 StartY=1.56045 StartZ=0 EndX=27.3142 EndY=3 EndZ=0
    g5: LineSegment [constr] StartX=27.3142 StartY=-1.56045 StartZ=0 EndX=27.3142 EndY=-3 EndZ=0
  constraints (16):
    c: Coincident(g0,g1)
    c: Coincident(g1,g2)
    c: Coincident(g2,g3)
    c: Coincident(g3,g0)
    c: Vertical(g0)
    c: Vertical(g2)
    c: Horizontal(g1)
    c: Horizontal(g3)
    c: PointOnObject(g-3,g0)
    c: Coincident(g4,g-3)
    c: Coincident(g4,g0)
    c: Coincident(g5,g-3)
    c: Coincident(g5,g0)
    c: Equal(g4,g5)
    c: Distance(g0,g0) = 6
    c: DistanceX(g3,g3) = 8
FEATURE [PartDesign::Pad] Pad037
  BaseFeature = -> Pad036
  Direction = (0,0,1)
  Length = 7
  Length2 = 10
  Profile = -> Sketch052
  ReferenceAxis = -> Sketch052 [N_Axis]
  Refine = true
  SideType = 0
  Suppressed = false
  Type = 0
  Type2 = 0
FEATURE [Sketcher::SketchObject] Sketch053
  ArcFitTolerance = 1e-06
  AttachmentSupport = -> [Pad037]
  ExternalGeometry = -> [Pad037]
  ExternalTypes = [0,0,0,0]
  FullyConstrained = true
  MakeInternals = false
  MapMode = 5
  Placement = pos=(35.3142,0,0) rot=(0.57735,0.57735,0.57735;2.0944rad)
  sketch-geometry (3):
    g0: LineSegment [constr] StartX=3 StartY=34.4 StartZ=0 EndX=-3 EndY=41.4 EndZ=0
    g1: GeomPoint [constr] X=1.99296e-11 Y=37.9 Z=0
    g2: Circle CenterX=1.99296e-11 CenterY=37.9 CenterZ=0 NormalX=0 NormalY=0 NormalZ=1 AngleXU=0 Radius=2.775
  constraints (5):
    c: Coincident(g0,g-5)
    c: Coincident(g0,g-6)
    c: Symmetric(g0,g0,g1)
    c: Diameter(g2) = 5.55
    c: Coincident(g2,g1)
FEATURE [PartDesign::Pocket] Pocket010
  BaseFeature = -> Pad037
  Direction = (-1,0,0)
  Length = 2
  Length2 = 5
  Profile = -> Sketch053
  ReferenceAxis = -> Sketch053 [N_Axis]
  Refine = true
  SideType = 0
  Suppressed = false
  Type = 0
  Type2 = 0
FEATURE [Sketcher::SketchObject] Sketch054
  ArcFitTolerance = 1e-06
  AttachmentSupport = -> [Pocket010]
  ExternalGeometry = -> [Pocket010]
  ExternalTypes = [0]
  FullyConstrained = true
  MakeInternals = false
  MapMode = 5
  Placement = pos=(33.3142,0,0) rot=(0.57735,0.57735,0.57735;2.0944rad)
  sketch-geometry (1):
    g0: Circle CenterX=0 CenterY=37.9 CenterZ=0 NormalX=0 NormalY=0 NormalZ=1 AngleXU=0 Radius=2.45
  constraints (2):
    c: Diameter(g0) = 4.9
    c: Coincident(g0,g-3)
FEATURE [PartDesign::Pocket] Pocket011
  BaseFeature = -> Pocket010
  Direction = (-1,0,0)
  Length = 5
  Length2 = 5
  Profile = -> Sketch054
  ReferenceAxis = -> Sketch054 [N_Axis]
  Refine = true
  SideType = 0
  Suppressed = false
  Type = 1
  Type2 = 0
FEATURE [PartDesign::Fillet] Fillet008
  Base = -> Pocket011 [Edge22,Edge24,Edge20,Edge18,Edge4,Edge2]
  BaseFeature = -> Pocket011
  Radius = 1
  Refine = true
  SupportTransform = false
  Suppressed = false
  UseAllEdges = false
FEATURE [Sketcher::SketchObject] Sketch057
  ArcFitTolerance = 1e-06
  AttachmentSupport = -> [Pocket011]
  ExternalGeometry = -> [Pocket011]
  ExternalTypes = [0,0,0]
  FullyConstrained = false
  MakeInternals = false
  MapMode = 5
  Placement = pos=(35.3142,0,0) rot=(0.57735,0.57735,0.57735;2.0944rad)
  sketch-geometry (10):
    g0: LineSegment [constr] StartX=3 StartY=34.4 StartZ=0 EndX=-3 EndY=41.4 EndZ=0
    g1: GeomPoint [constr] X=1.99294e-11 Y=37.9 Z=0
    g2: LineSegment StartX=4.04081 StartY=38.9 StartZ=0 EndX=1.95919 EndY=38.9 EndZ=0
    g3: LineSegment StartX=1.95919 StartY=38.9 StartZ=0 EndX=1.95919 EndY=36.9 EndZ=0
    g4: LineSegment StartX=1.95919 StartY=36.9 StartZ=0 EndX=4.04081 EndY=36.9 EndZ=0
    g5: LineSegment StartX=4.04081 StartY=36.9 StartZ=0 EndX=4.04081 EndY=38.9 EndZ=0
    g6: GeomPoint X=1.95919 Y=37.9 Z=0
    g7: LineSegment [constr] StartX=1.95919 StartY=37.9 StartZ=0 EndX=1.99294e-11 EndY=37.9 EndZ=0
    g8: LineSegment [constr] StartX=4.04081 StartY=38.9 StartZ=0 EndX=3 EndY=41.4 EndZ=0
    g9: LineSegment [constr] StartX=1.95919 StartY=38.9 StartZ=0 EndX=3 EndY=41.4 EndZ=0
  constraints (21):
    c: Coincident(g0,g-4)
    c: Coincident(g0,g-3)
    c: Symmetric(g0,g0,g1)
    c: Coincident(g2,g3)
    c: Coincident(g3,g4)
    c: Coincident(g4,g5)
    c: Coincident(g5,g2)
    c: Horizontal(g2)
    c: Horizontal(g4)
    c: Vertical(g3)
    c: Vertical(g5)
    c: Distance(g2,g4) = 2
    c: Symmetric(g3,g3,g6)
    c: Coincident(g7,g6)
    c: Coincident(g7,g1)
    c: Horizontal(g7)
    c: Coincident(g8,g2)
    c: Coincident(g8,g-5)
    c: Coincident(g9,g2)
    c: Coincident(g9,g8)
    c: Equal(g8,g9)
FEATURE [PartDesign::Pocket] Pocket014
  BaseFeature = -> Fillet008
  Direction = (-1,0,0)
  Length = 5
  Length2 = 5
  Profile = -> Sketch057
  ReferenceAxis = -> Sketch057 [N_Axis]
  Refine = true
  SideType = 0
  Suppressed = false
  Type = 1
  Type2 = 0
FEATURE [PartDesign::Body] Body010  label="rgb_holder"
  AllowCompound = false
  Group = -> [Binder015,Sketch051,Pad036,Sketch052,Pad037,Sketch053,Pocket010,Sketch054,Pocket011,Fillet008,Sketch057,Pocket014]
  Origin = -> Origin023
  Tip = -> Pocket014
COMPONENT P7 — recipe-attached ("photodiode_holder", modeled in this document).
Construction recipe (the document's own serialized feature program — sketch geometry with constraints, then the solid features built on it; lengths are millimeters unless a unit is written):

FEATURE [PartDesign::FeatureBase] Clone
  BaseFeature = -> Pad037
  Suppressed = false
FEATURE [Sketcher::SketchObject] Sketch055
  ArcFitTolerance = 1e-06
  AttachmentSupport = -> [Clone]
  ExternalGeometry = -> [Clone]
  ExternalTypes = [0,0,0,0]
  FullyConstrained = true
  MakeInternals = false
  MapMode = 5
  Placement = pos=(35.3142,0,0) rot=(0.57735,0.57735,0.57735;2.0944rad)
  sketch-geometry (3):
    g0: LineSegment [constr] StartX=3 StartY=34.4 StartZ=0 EndX=-3 EndY=41.4 EndZ=0
    g1: Circle CenterX=1.99299e-11 CenterY=37.9 CenterZ=0 NormalX=0 NormalY=0 NormalZ=1 AngleXU=0 Radius=2.9
    g2: GeomPoint X=1.99299e-11 Y=37.9 Z=0
  constraints (5):
    c: Coincident(g0,g-6)
    c: Coincident(g0,g-4)
    c: Diameter(g1) = 5.8
    c: Symmetric(g0,g0,g2)
    c: Coincident(g1,g2)
FEATURE [PartDesign::Pocket] Pocket012
  BaseFeature = -> Clone
  Direction = (-1,0,0)
  Length = 2
  Length2 = 5
  Profile = -> Sketch055
  ReferenceAxis = -> Sketch055 [N_Axis]
  Refine = true
  SideType = 0
  Suppressed = false
  Type = 0
  Type2 = 0
FEATURE [Sketcher::SketchObject] Sketch056
  ArcFitTolerance = 1e-06
  AttachmentSupport = -> [Pocket012]
  ExternalGeometry = -> [Pocket012]
  ExternalTypes = [0]
  FullyConstrained = true
  MakeInternals = false
  MapMode = 5
  Placement = pos=(33.3142,0,0) rot=(0.57735,0.57735,0.57735;2.0944rad)
  sketch-geometry (1):
    g0: Circle CenterX=0 CenterY=37.9 CenterZ=0 NormalX=0 NormalY=0 NormalZ=1 AngleXU=0 Radius=2.5
  constraints (2):
    c: Diameter(g0) = 5
    c: Coincident(g0,g-3)
FEATURE [PartDesign::Pocket] Pocket013
  BaseFeature = -> Pocket012
  Direction = (-1,0,0)
  Length = 5
  Length2 = 5
  Profile = -> Sketch056
  ReferenceAxis = -> Sketch056 [N_Axis]
  Refine = true
  SideType = 0
  Suppressed = false
  Type = 1
  Type2 = 0
FEATURE [PartDesign::Fillet] Fillet009
  Base = -> Pocket013 [Edge22,Edge24,Edge18,Edge20,Edge2,Edge4]
  BaseFeature = -> Pocket013
  Radius = 1
  Refine = true
  SupportTransform = false
  Suppressed = false
  UseAllEdges = false
FEATURE [Sketcher::SketchObject] Sketch058
  ArcFitTolerance = 1e-06
  AttachmentSupport = -> [Pocket013]
  ExternalGeometry = -> [Pocket013]
  ExternalTypes = [0,0,0,0]
  FullyConstrained = false
  MakeInternals = false
  MapMode = 5
  Placement = pos=(35.3142,0,0) rot=(0.57735,0.57735,0.57735;2.0944rad)
  sketch-geometry (8):
    g0: LineSegment [constr] StartX=3 StartY=34.4 StartZ=0 EndX=-3 EndY=41.4 EndZ=0
    g1: GeomPoint [constr] X=1.99295e-11 Y=37.9 Z=0
    g2: GeomPoint [constr] X=3 Y=37.9 Z=0
    g3: LineSegment StartX=1.81397 StartY=36.9 StartZ=0 EndX=4.18603 EndY=36.9 EndZ=0
    g4: LineSegment StartX=4.18603 StartY=36.9 StartZ=0 EndX=4.18603 EndY=38.9 EndZ=0
    g5: LineSegment StartX=4.18603 StartY=38.9 StartZ=0 EndX=1.81397 EndY=38.9 EndZ=0
    g6: LineSegment StartX=1.81397 StartY=38.9 StartZ=0 EndX=1.81397 EndY=36.9 EndZ=0
    g7: GeomPoint [constr] X=3 Y=37.9 Z=0
  constraints (15):
    c: Coincident(g0,g-6)
    c: Coincident(g0,g-4)
    c: Symmetric(g0,g0,g1)
    c: Symmetric(g-6,g-6,g2)
    c: Coincident(g3,g4)
    c: Coincident(g4,g5)
    c: Coincident(g5,g6)
    c: Coincident(g6,g3)
    c: Horizontal(g3)
    c: Horizontal(g5)
    c: Vertical(g4)
    c: Vertical(g6)
    c: Symmetric(g5,g3,g7)
    c: Distance(g3,g5) = 2
    c: Coincident(g7,g2)
FEATURE [PartDesign::Pocket] Pocket015
  BaseFeature = -> Fillet009
  Direction = (-1,0,0)
  Length = 5
  Length2 = 5
  Profile = -> Sketch058
  ReferenceAxis = -> Sketch058 [N_Axis]
  Refine = true
  SideType = 0
  Suppressed = false
  Type = 1
  Type2 = 0
FEATURE [Sketcher::SketchObject] Sketch059
  ArcFitTolerance = 1e-06
  AttachmentSupport = -> [Pocket015]
  ExternalGeometry = -> [Pocket015]
  ExternalTypes = [0,0,0,0]
  FullyConstrained = true
  MakeInternals = false
  MapMode = 5
  Placement = pos=(0,0,41.4) rot=(0,0,1;0rad)
  sketch-geometry (7):
    g0: LineSegment StartX=27.3142 StartY=-0.5 StartZ=0 EndX=27.3142 EndY=0.5 EndZ=0
    g1: LineSegment StartX=27.3142 StartY=0.5 StartZ=0 EndX=28.3142 EndY=0.5 EndZ=0
    g2: LineSegment StartX=28.3142 StartY=0.5 StartZ=0 EndX=28.3142 EndY=-0.5 EndZ=0
    g3: LineSegment StartX=28.3142 StartY=-0.5 StartZ=0 EndX=27.3142 EndY=-0.5 EndZ=0
    g4: LineSegment [constr] StartX=35.3142 StartY=-2 StartZ=0 EndX=27.3142 EndY=2 EndZ=0
    g5: LineSegment [constr] StartX=27.3142 StartY=2 StartZ=0 EndX=27.3142 EndY=-2 EndZ=0
    g6: GeomPoint [constr] X=27.3142 Y=3.08695e-11 Z=0
  constraints (16):
    c: Coincident(g0,g1)
    c: Coincident(g1,g2)
    c: Coincident(g2,g3)
    c: Coincident(g3,g0)
    c: Vertical(g0)
    c: Vertical(g2)
    c: Horizontal(g1)
    c: Horizontal(g3)
    c: Coincident(g4,g-6)
    c: Coincident(g4,g-5)
    c: DistanceX(g1,g1) = 1
    c: DistanceY(g2,g2) = 1
    c: Coincident(g5,g4)
    c: Coincident(g5,g-6)
    c: Symmetric(g5,g5,g6)
    c: Symmetric(g0,g0,g6)
FEATURE [PartDesign::Pad] Pad038
  BaseFeature = -> Pocket015
  Direction = (0,0,1)
  Length = 1
  Length2 = 10
  Profile = -> Sketch059
  ReferenceAxis = -> Sketch059 [N_Axis]
  Refine = true
  SideType = 0
  Suppressed = false
  Type = 0
  Type2 = 0
FEATURE [PartDesign::Body] Body011  label="photodiode_holder"
  AllowCompound = false
  Group = -> [Clone,Sketch055,Pocket012,Sketch056,Pocket013,Fillet009,Sketch058,Pocket015,Sketch059,Pad038]
  Origin = -> Origin025
  Tip = -> Pad038
COMPONENT P8 — recipe-attached ("laser_diode_holder", modeled in this document).
Construction recipe (the document's own serialized feature program — sketch geometry with constraints, then the solid features built on it; lengths are millimeters unless a unit is written):

FEATURE [PartDesign::SubShapeBinder] Binder016
  BindCopyOnChange = 0
  BindMode = 0
  ClaimChildren = false
  Context = -> Body012 [Binder016.]
  Fuse = false
  MakeFace = true
  OffsetFill = false
  OffsetIntersection = false
  OffsetJoinType = 0
  OffsetOpenResult = false
  PartialLoad = false
  Refine = true
  Relative = true
  _Version = 2
FEATURE [PartDesign::SubShapeBinder] Binder017
  BindCopyOnChange = 0
  BindMode = 0
  ClaimChildren = false
  Context = -> Body012 [Binder017.]
  Fuse = false
  MakeFace = true
  OffsetFill = false
  OffsetIntersection = false
  OffsetJoinType = 0
  OffsetOpenResult = false
  PartialLoad = false
  Refine = true
  Relative = true
  _Version = 2
FEATURE [Sketcher::SketchObject] Sketch060
  ArcFitTolerance = 1e-06
  AttachmentSupport = -> [Binder016]
  ExternalGeometry = -> [Binder017,Binder016]
  ExternalTypes = [0,0,0,0]
  FullyConstrained = true
  MakeInternals = false
  MapMode = 5
  Placement = pos=(1.723e-13,0,118) rot=(0,0,1;0rad)
  sketch-geometry (4):
    g0: LineSegment StartX=-80.5314 StartY=-53.7373 StartZ=0 EndX=-12.1314 EndY=-53.7373 EndZ=0
    g1: LineSegment StartX=-12.1314 StartY=-53.7373 StartZ=0 EndX=-12.1314 EndY=-1.73726 EndZ=0
    g2: LineSegment StartX=-12.1314 StartY=-1.73726 StartZ=0 EndX=-80.5314 EndY=-1.73726 EndZ=0
    g3: LineSegment StartX=-80.5314 StartY=-1.73726 StartZ=0 EndX=-80.5314 EndY=-53.7373 EndZ=0
  constraints (12):
    c: Horizontal(g0)
    c: Coincident(g1,g0)
    c: Vertical(g1)
    c: Coincident(g2,g1)
    c: Horizontal(g2)
    c: Coincident(g3,g2)
    c: Coincident(g3,g0)
    c: Vertical(g3)
    c: PointOnObject(g-4,g1)
    c: PointOnObject(g-5,g0)
    c: Distance(g-5,g3) = 4
    c: Distance(g-6,g2) = 4
FEATURE [PartDesign::Pad] Pad039
  Direction = (1.5e-15,0,1)
  Length = 4
  Length2 = 10
  Profile = -> Sketch060
  ReferenceAxis = -> Sketch060 [N_Axis]
  Refine = true
  SideType = 0
  Suppressed = false
  Type = 0
  Type2 = 0
FEATURE [Sketcher::SketchObject] Sketch061
  ArcFitTolerance = 1e-06
  AttachmentSupport = -> [Pad039]
  ExternalGeometry = -> [Pad039,Binder016]
  ExternalTypes = [0,0,0,0,0,0,0]
  FullyConstrained = true
  MakeInternals = false
  MapMode = 5
  Placement = pos=(1.711e-13,0,118) rot=(1,0,0;3.14159rad)
  sketch-geometry (12):
    g0: LineSegment StartX=-76.5314 StartY=1.73726 StartZ=0 EndX=-76.5314 EndY=53.7373 EndZ=0
    g1: LineSegment StartX=-76.5314 StartY=53.7373 StartZ=0 EndX=-80.5314 EndY=53.7373 EndZ=0
    g2: LineSegment StartX=-80.5314 StartY=53.7373 StartZ=0 EndX=-80.5314 EndY=1.73726 EndZ=0
    g3: LineSegment StartX=-80.5314 StartY=1.73726 StartZ=0 EndX=-76.5314 EndY=1.73726 EndZ=0
    g4: LineSegment StartX=-72.5314 StartY=5.73726 StartZ=0 EndX=-72.5314 EndY=1.73726 EndZ=0
    g5: LineSegment StartX=-72.5314 StartY=1.73726 StartZ=0 EndX=-68.5314 EndY=1.73726 EndZ=0
    g6: LineSegment StartX=-68.5314 StartY=1.73726 StartZ=0 EndX=-68.5314 EndY=5.73726 EndZ=0
    g7: LineSegment StartX=-68.5314 StartY=5.73726 StartZ=0 EndX=-72.5314 EndY=5.73726 EndZ=0
    g8: LineSegment StartX=-68.5314 StartY=49.7373 StartZ=0 EndX=-64.5314 EndY=49.7373 EndZ=0
    g9: LineSegment StartX=-64.5314 StartY=49.7373 StartZ=0 EndX=-64.5314 EndY=53.7373 EndZ=0
    g10: LineSegment StartX=-64.5314 StartY=53.7373 StartZ=0 EndX=-68.5314 EndY=53.7373 EndZ=0
    g11: LineSegment StartX=-68.5314 StartY=53.7373 StartZ=0 EndX=-68.5314 EndY=49.7373 EndZ=0
  constraints (30):
    c: Coincident(g0,g1)
    c: Coincident(g1,g2)
    c: Coincident(g2,g3)
    c: Coincident(g3,g0)
    c: Vertical(g0)
    c: Horizontal(g3)
    c: Coincident(g4,g5)
    c: Coincident(g5,g6)
    c: Coincident(g6,g7)
    c: Coincident(g7,g4)
    c: Vertical(g4)
    c: Vertical(g6)
    c: Horizontal(g5)
    c: Coincident(g4,g-9)
    c: PointOnObject(g5,g-4)
    c: Coincident(g6,g-9)
    c: Coincident(g8,g9)
    c: Coincident(g9,g10)
    c: Coincident(g10,g11)
    c: Coincident(g11,g8)
    c: Horizontal(g8)
    c: Horizontal(g10)
    c: Vertical(g9)
    c: Vertical(g11)
    c: Distance(g9,g11) = 4
    c: Coincident(g8,g-7)
    c: PointOnObject(g9,g-6)
    c: Coincident(g0,g-5)
    c: Coincident(g1,g-6)
    c: Coincident(g-4,g2)
FEATURE [PartDesign::Pad] Pad040
  BaseFeature = -> Pad039
  Direction = (-1.5e-15,0,-1)
  Length = 10
  Length2 = 10
  Profile = -> Sketch061
  ReferenceAxis = -> Sketch061 [N_Axis]
  Refine = true
  SideType = 0
  Suppressed = false
  Type = 0
  Type2 = 0
FEATURE [Sketcher::SketchObject] Sketch066
  ArcFitTolerance = 1e-06
  AttachmentSupport = -> [Pad040]
  ExternalGeometry = -> [Pad040]
  ExternalTypes = [0,0,0]
  FullyConstrained = true
  MakeInternals = false
  MapMode = 5
  Placement = pos=(1.769e-13,0,122) rot=(0,0,1;0rad)
  sketch-geometry (4):
    g0: LineSegment StartX=-12.1314 StartY=-1.73726 StartZ=0 EndX=-16.1314 EndY=-1.73726 EndZ=0
    g1: LineSegment StartX=-16.1314 StartY=-1.73726 StartZ=0 EndX=-16.1314 EndY=-53.7373 EndZ=0
    g2: LineSegment StartX=-16.1314 StartY=-53.7373 StartZ=0 EndX=-12.1314 EndY=-53.7373 EndZ=0
    g3: LineSegment StartX=-12.1314 StartY=-53.7373 StartZ=0 EndX=-12.1314 EndY=-1.73726 EndZ=0
  constraints (10):
    c: Coincident(g0,g1)
    c: Coincident(g1,g2)
    c: Coincident(g2,g3)
    c: Coincident(g3,g0)
    c: Horizontal(g0)
    c: Horizontal(g2)
    c: Vertical(g1)
    c: Distance(g1,g3) = 4
    c: Coincident(g0,g-4)
    c: Coincident(g-5,g2)
FEATURE [PartDesign::Pad] Pad043
  BaseFeature = -> Pad040
  Direction = (1.5e-15,0,1)
  Length = 15
  Length2 = 10
  Profile = -> Sketch066
  ReferenceAxis = -> Sketch066 [N_Axis]
  Refine = true
  Reversed = true
  SideType = 0
  Suppressed = false
  Type = 0
  Type2 = 0
FEATURE [Sketcher::SketchObject] Sketch067
  ArcFitTolerance = 1e-06
  AttachmentSupport = -> [Pad043]
  ExternalGeometry = -> [Pad043,Binder017]
  ExternalTypes = [0,0,0,0]
  FullyConstrained = true
  MakeInternals = false
  MapMode = 5
  Placement = pos=(-12.1314,0,2.81e-14) rot=(0.57735,0.57735,0.57735;2.0944rad)
  sketch-geometry (8):
    g0: LineSegment StartX=-46.3686 StartY=107 StartZ=0 EndX=-46.3686 EndY=122 EndZ=0
    g1: LineSegment StartX=-46.3686 StartY=122 StartZ=0 EndX=-42.3686 EndY=122 EndZ=0
    g2: LineSegment StartX=-42.3686 StartY=122 StartZ=0 EndX=-42.3686 EndY=107 EndZ=0
    g3: LineSegment StartX=-42.3686 StartY=107 StartZ=0 EndX=-46.3686 EndY=107 EndZ=0
    g4: LineSegment StartX=-13.3686 StartY=107 StartZ=0 EndX=-17.3686 EndY=107 EndZ=0
    g5: LineSegment StartX=-17.3686 StartY=107 StartZ=0 EndX=-17.3686 EndY=122 EndZ=0
    g6: LineSegment StartX=-17.3686 StartY=122 StartZ=0 EndX=-13.3686 EndY=122 EndZ=0
    g7: LineSegment StartX=-13.3686 StartY=122 StartZ=0 EndX=-13.3686 EndY=107 EndZ=0
  constraints (24):
    c: Coincident(g0,g1)
    c: Coincident(g1,g2)
    c: Coincident(g2,g3)
    c: Coincident(g3,g0)
    c: Vertical(g0)
    c: Vertical(g2)
    c: Horizontal(g1)
    c: Horizontal(g3)
    c: PointOnObject(g0,g-3)
    c: PointOnObject(g-4,g2)
    c: Distance(g3,g3) = 4
    c: Coincident(g4,g5)
    c: Coincident(g5,g6)
    c: Coincident(g6,g7)
    c: Coincident(g7,g4)
    c: Horizontal(g4)
    c: Horizontal(g6)
    c: Vertical(g5)
    c: Vertical(g7)
    c: PointOnObject(g4,g-3)
    c: PointOnObject(g-5,g5)
    c: Distance(g4,g4) = 4
    c: PointOnObject(g1,g-6)
    c: PointOnObject(g6,g-6)
FEATURE [PartDesign::Pad] Pad044
  BaseFeature = -> Pad043
  Direction = (1,0,-2.2e-15)
  Length = 5
  Length2 = 10
  Profile = -> Sketch067
  ReferenceAxis = -> Sketch067 [N_Axis]
  Refine = true
  SideType = 0
  Suppressed = false
  Type = 0
  Type2 = 0
FEATURE [PartDesign::Chamfer] Chamfer
  Angle = 45
  Base = -> Pad044 [Edge36,Edge35]
  BaseFeature = -> Pad044
  ChamferType = 0
  FlipDirection = false
  Refine = true
  Size = 6
  Size2 = 1
  SupportTransform = false
  Suppressed = false
  UseAllEdges = false
FEATURE [PartDesign::Chamfer] Chamfer001
  Angle = 45
  Base = -> Chamfer [Edge44,Edge79]
  BaseFeature = -> Chamfer
  ChamferType = 0
  FlipDirection = false
  Refine = true
  Size = 3
  Size2 = 1
  SupportTransform = false
  Suppressed = false
  UseAllEdges = false
FEATURE [PartDesign::Body] Body012  label="laser_diode_holder"
  AllowCompound = false
  Group = -> [Sketch060,Pad039,Sketch061,Pad040,Sketch066,Pad043,Sketch067,Pad044,Binder016,Binder017,Chamfer,Chamfer001]
  Origin = -> Origin027
  Tip = -> Chamfer001
COMPONENT P9 — recipe-attached ("laser_diode", modeled in this document).
Construction recipe (the document's own serialized feature program — sketch geometry with constraints, then the solid features built on it; lengths are millimeters unless a unit is written):

FEATURE [Sketcher::SketchObject] Sketch063
  ArcFitTolerance = 1e-06
  AttachmentSupport = -> [Origin029]
  ExternalTypes = [0]
  FullyConstrained = true
  MakeInternals = false
  MapMode = 5
  Placement = pos=(0,0,0) rot=(1,0,0;1.5708rad)
  sketch-geometry (4):
    g0: LineSegment StartX=0 StartY=0 StartZ=0 EndX=25 EndY=0 EndZ=0
    g1: LineSegment StartX=25 StartY=0 StartZ=0 EndX=25 EndY=20 EndZ=0
    g2: LineSegment StartX=25 StartY=20 StartZ=0 EndX=0 EndY=20 EndZ=0
    g3: LineSegment StartX=0 StartY=20 StartZ=0 EndX=0 EndY=0 EndZ=0
  constraints (11):
    c: Coincident(g0,g1)
    c: Coincident(g1,g2)
    c: Coincident(g2,g3)
    c: Coincident(g3,g0)
    c: Horizontal(g0)
    c: Horizontal(g2)
    c: Vertical(g1)
    c: Vertical(g3)
    c: Distance(g1,g3) = 25
    c: Distance(g0,g2) = 20
    c: Coincident(g0,g-1)
FEATURE [PartDesign::Pad] Pad042
  Direction = (0,-1,2e-16)
  Length = 16
  Length2 = 10
  Profile = -> Sketch063
  ReferenceAxis = -> Sketch063 [N_Axis]
  Refine = true
  SideType = 0
  Suppressed = false
  Type = 0
  Type2 = 0
FEATURE [Sketcher::SketchObject] Sketch064
  ArcFitTolerance = 1e-06
  AttachmentSupport = -> [Pad042]
  ExternalGeometry = -> [Pad042]
  ExternalTypes = [0]
  FullyConstrained = true
  MakeInternals = false
  MapMode = 5
  Placement = pos=(0,-16,0) rot=(1,0,0;1.5708rad)
  sketch-geometry (5):
    g0: GeomPoint [constr] X=12.5 Y=3.6e-15 Z=0
    g1: LineSegment [constr] StartX=12.5 StartY=3.6e-15 StartZ=0 EndX=12.5 EndY=10 EndZ=0
    g2: Circle CenterX=12.5 CenterY=12 CenterZ=0 NormalX=0 NormalY=0 NormalZ=1 AngleXU=0 Radius=2
    g3: LineSegment [constr] StartX=12.5 StartY=10 StartZ=0 EndX=12.5 EndY=12 EndZ=0
    g4: GeomPoint [constr] X=12.5 Y=12 Z=0
  constraints (10):
    c: Symmetric(g-3,g-3,g0)
    c: Distance(g1) = 10
    c: Angle(g-1,g1) = 1.5708
    c: Coincident(g1,g0)
    c: Diameter(g2) = 4
    c: PointOnObject(g1,g2)
    c: Coincident(g3,g1)
    c: Coincident(g3,g2)
    c: Vertical(g3)
    c: Coincident(g4,g2)
FEATURE [PartDesign::Pocket] Pocket016
  BaseFeature = -> Pad042
  Direction = (0,1,-2e-16)
  Length = 5
  Length2 = 5
  Profile = -> Sketch064
  ReferenceAxis = -> Sketch064 [N_Axis]
  Refine = true
  SideType = 0
  Suppressed = false
  Type = 0
  Type2 = 0
FEATURE [Sketcher::SketchObject] Sketch065
  ArcFitTolerance = 1e-06
  AttachmentSupport = -> [Pocket016]
  ExternalGeometry = -> [Pocket016]
  ExternalTypes = [0,0,0]
  FullyConstrained = true
  MakeInternals = false
  MapMode = 5
  Placement = pos=(0,-16,0) rot=(1,0,0;1.5708rad)
  sketch-geometry (12):
    g0: LineSegment [constr] StartX=25 StartY=9e-16 StartZ=0 EndX=20 EndY=9e-16 EndZ=0
    g1: LineSegment [constr] StartX=20 StartY=9e-16 StartZ=0 EndX=20 EndY=5 EndZ=0
    g2: LineSegment StartX=20 StartY=5 StartZ=0 EndX=25 EndY=5 EndZ=0
    g3: LineSegment StartX=25 StartY=5 StartZ=0 EndX=25 EndY=20 EndZ=0
    g4: LineSegment StartX=25 StartY=20 StartZ=0 EndX=20 EndY=20 EndZ=0
    g5: LineSegment StartX=20 StartY=20 StartZ=0 EndX=20 EndY=5 EndZ=0
    g6: LineSegment [constr] StartX=0 StartY=9e-16 StartZ=0 EndX=5 EndY=9e-16 EndZ=0
    g7: LineSegment [constr] StartX=5 StartY=9e-16 StartZ=0 EndX=5 EndY=5 EndZ=0
    g8: LineSegment StartX=5 StartY=5 StartZ=0 EndX=5 EndY=20 EndZ=0
    g9: LineSegment StartX=5 StartY=20 StartZ=0 EndX=0 EndY=20 EndZ=0
    g10: LineSegment StartX=0 StartY=20 StartZ=0 EndX=0 EndY=5 EndZ=0
    g11: LineSegment StartX=0 StartY=5 StartZ=0 EndX=5 EndY=5 EndZ=0
  constraints (32):
    c: Distance(g0) = 5
    c: Coincident(g0,g-5)
    c: PointOnObject(g0,g-4)
    c: Distance(g1) = 5
    c: Angle(g-1,g1) = 1.5708
    c: Coincident(g1,g0)
    c: Coincident(g2,g3)
    c: Coincident(g3,g4)
    c: Coincident(g4,g5)
    c: Coincident(g5,g2)
    c: Horizontal(g2)
    c: Horizontal(g4)
    c: Vertical(g3)
    c: Vertical(g5)
    c: Coincident(g2,g1)
    c: Coincident(g3,g-5)
    c: Distance(g6) = 5
    c: Coincident(g6,g-4)
    c: PointOnObject(g6,g-4)
    c: Distance(g7) = 5
    c: Angle(g-1,g7) = 1.5708
    c: Coincident(g7,g6)
    c: Coincident(g8,g9)
    c: Coincident(g9,g10)
    c: Coincident(g10,g11)
    c: Coincident(g11,g8)
    c: Vertical(g8)
    c: Vertical(g10)
    c: Horizontal(g9)
    c: Horizontal(g11)
    c: Coincident(g8,g7)
    c: Coincident(g9,g-3)
FEATURE [PartDesign::Pocket] Pocket017
  BaseFeature = -> Pocket016
  Direction = (0,1,-2e-16)
  Length = 5
  Length2 = 5
  Profile = -> Sketch065
  ReferenceAxis = -> Sketch065 [N_Axis]
  Refine = true
  SideType = 0
  Suppressed = false
  Type = 1
  Type2 = 0
FEATURE [Sketcher::SketchObject] Sketch069
  ArcFitTolerance = 1e-06
  AttachmentSupport = -> [Pocket017]
  ExternalGeometry = -> [Pocket017]
  ExternalTypes = [0]
  FullyConstrained = true
  MakeInternals = false
  MapMode = 5
  Placement = pos=(0,-16,0) rot=(1,0,0;1.5708rad)
  sketch-geometry (1):
    g0: GeomPoint X=12.5 Y=12 Z=0
  constraints (1):
    c: Coincident(g0,g-3)
FEATURE [PartDesign::Body] Body013  label="laser_diode"
  AllowCompound = false
  Group = -> [Sketch063,Pad042,Sketch064,Pocket016,Sketch065,Pocket017,Sketch069]
  Origin = -> Origin029
  Tip = -> Pocket017
COMPONENT P10 — recipe-attached ("mirrors_with_points_and_lines", modeled in this document).
Construction recipe (the document's own serialized feature program — sketch geometry with constraints, then the solid features built on it; lengths are millimeters unless a unit is written):

FEATURE [PartDesign::FeatureBase] Clone005
  BaseFeature = -> Fusion
  Placement = pos=(0,0,0) rot=(0,0,1;4.71239rad)
  Suppressed = false
FEATURE [Sketcher::SketchObject] Sketch068
  ArcFitTolerance = 1e-06
  AttachmentOffset = pos=(0,0,7.5) rot=(0,0,1;0rad)
  AttachmentSupport = -> [Clone005]
  ExternalGeometry = -> [Clone005]
  ExternalTypes = [0,0]
  FullyConstrained = true
  MakeInternals = false
  MapMode = 5
  Placement = pos=(0,0,61.9) rot=(0,0,-1;1.5708rad)
  sketch-geometry (5):
    g0: LineSegment [constr] StartX=-5.43467 StartY=-5.17193 StartZ=0 EndX=5.17193 EndY=5.43467 EndZ=0
    g1: GeomPoint [constr] X=-0.131371 Y=0.131371 Z=0
    g2: LineSegment StartX=-0.131371 StartY=0.131371 StartZ=0 EndX=99.8686 EndY=0.131371 EndZ=0
    g3: LineSegment StartX=-0.131371 StartY=0.131371 StartZ=0 EndX=-0.131371 EndY=-99.8686 EndZ=0
    g4: LineSegment StartX=-0.131371 StartY=0.131371 StartZ=0 EndX=70.5793 EndY=-70.5793 EndZ=0
  constraints (13):
    c: PointOnObject(g0,g-3)
    c: Symmetric(g0,g0,g1)
    c: Coincident(g0,g-4)
    c: Coincident(g2,g1)
    c: Coincident(g3,g1)
    c: Angle(g3,g2) = 1.5708
    c: Parallel(g0,g-4)
    c: DistanceX(g2,g2) = 100
    c: DistanceY(g3,g3) = 100
    c: Angle(g0,g3) = 0.785398
    c: Distance(g4) = 100
    c: Coincident(g4,g1)
    c: Angle(g3,g4) = 0.785398
FEATURE [PartDesign::Body] Body014  label="mirrors_with_points_and_lines"
  AllowCompound = false
  Group = -> [Clone005,Sketch068]
  Origin = -> Origin031
  Tip = -> Clone005
COMPONENT P11 — recipe-attached ("spring_test", modeled in this document).
Construction recipe (the document's own serialized feature program — sketch geometry with constraints, then the solid features built on it; lengths are millimeters unless a unit is written):

FEATURE [Sketcher::SketchObject] Sketch077
  ArcFitTolerance = 1e-06
  AttachmentSupport = -> [Origin036]
  ExternalTypes = [0]
  FullyConstrained = true
  MakeInternals = false
  MapMode = 5
  sketch-geometry (6):
    g0: Circle CenterX=0 CenterY=-1e-16 CenterZ=0 NormalX=0 NormalY=0 NormalZ=1 AngleXU=0 Radius=8
    g1: LineSegment StartX=-4 StartY=-4 StartZ=0 EndX=4 EndY=-4 EndZ=0
    g2: LineSegment StartX=4 StartY=-4 StartZ=0 EndX=4 EndY=4 EndZ=0
    g3: LineSegment StartX=4 StartY=4 StartZ=0 EndX=-4 EndY=4 EndZ=0
    g4: LineSegment StartX=-4 StartY=4 StartZ=0 EndX=-4 EndY=-4 EndZ=0
    g5: GeomPoint [constr] X=0 Y=-1e-16 Z=0
  constraints (14):
    c: Coincident(g0,g-1)
    c: Coincident(g1,g2)
    c: Coincident(g2,g3)
    c: Coincident(g3,g4)
    c: Coincident(g4,g1)
    c: Horizontal(g1)
    c: Horizontal(g3)
    c: Vertical(g2)
    c: Vertical(g4)
    c: Symmetric(g3,g1,g5)
    c: Coincident(g5,g0)
    c: Equal(g3,g2)
    c: Distance(g3,g3) = 8
    c: Diameter(g0) = 16
FEATURE [PartDesign::Pad] Pad050
  Direction = (0,0,1)
  Length = 2
  Length2 = 10
  Profile = -> Sketch077
  ReferenceAxis = -> Sketch077 [N_Axis]
  Refine = true
  SideType = 0
  Suppressed = false
  Type = 0
  Type2 = 0
FEATURE [Sketcher::SketchObject] Sketch078
  ArcFitTolerance = 1e-06
  AttachmentSupport = -> [Origin036]
  ExternalGeometry = -> [Pad050]
  ExternalTypes = [0]
  FullyConstrained = true
  MakeInternals = false
  MapMode = 5
  Placement = pos=(0,0,0) rot=(1,0,0;1.5708rad)
  sketch-geometry (4):
    g0: LineSegment StartX=8 StartY=2 StartZ=0 EndX=7.25 EndY=2 EndZ=0
    g1: LineSegment StartX=7.25 StartY=2 StartZ=0 EndX=7.25 EndY=0 EndZ=0
    g2: LineSegment StartX=7.25 StartY=0 StartZ=0 EndX=8 EndY=0 EndZ=0
    g3: LineSegment StartX=8 StartY=0 StartZ=0 EndX=8 EndY=2 EndZ=0
  constraints (11):
    c: Coincident(g0,g1)
    c: Coincident(g1,g2)
    c: Coincident(g2,g3)
    c: Coincident(g3,g0)
    c: Horizontal(g0)
    c: Horizontal(g2)
    c: Vertical(g1)
    c: Vertical(g3)
    c: Coincident(g0,g-3)
    c: PointOnObject(g1,g-1)
    c: Distance(g0,g0) = 0.75
FEATURE [PartDesign::AdditiveHelix] AdditiveHelix
  Angle = 0
  Axis = (0,2e-16,1)
  Base = (0,0,0)
  BaseFeature = -> Pad050
  Growth = 1.5
  HasBeenEdited = true
  Height = 0
  LeftHanded = false
  Mode = 3
  Outside = false
  Pitch = 0
  Profile = -> Sketch078
  ReferenceAxis = -> Sketch078 [V_Axis]
  Refine = true
  Suppressed = false
  Tolerance = 0.1
  Turns = 3.5
FEATURE [Sketcher::SketchObject] Sketch085
  ArcFitTolerance = 1e-06
  AttachmentSupport = -> [Origin036]
  ExternalGeometry = -> [AdditiveHelix]
  ExternalTypes = [0]
  FullyConstrained = true
  MakeInternals = false
  MapMode = 5
  sketch-geometry (2):
    g0: Circle CenterX=0 CenterY=0 CenterZ=0 NormalX=0 NormalY=0 NormalZ=1 AngleXU=0 Radius=12.5
    g1: Circle CenterX=0 CenterY=0 CenterZ=0 NormalX=0 NormalY=0 NormalZ=1 AngleXU=0 Radius=15.5
  constraints (4):
    c: Coincident(g0,g-1)
    c: PointOnObject(g-3,g0)
    c: Coincident(g1,g0)
    c: Distance(g0,g1) = 3
FEATURE [PartDesign::Pad] Pad056
  BaseFeature = -> AdditiveHelix
  Direction = (0,0,1)
  Length = 10
  Length2 = 10
  Profile = -> Sketch085
  ReferenceAxis = -> Sketch085 [N_Axis]
  Refine = true
  SideType = 0
  Suppressed = false
  Type = 3
  Type2 = 0
  UpToFace = -> AdditiveHelix [Face16]
FEATURE [PartDesign::Body] Body016  label="spring_test"
  AllowCompound = false
  Group = -> [Sketch077,Pad050,Sketch078,AdditiveHelix,Sketch085,Pad056]
  Origin = -> Origin036
  Tip = -> Pad056
COMPONENT P12 — recipe-attached ("spring", modeled in this document).
Construction recipe (the document's own serialized feature program — sketch geometry with constraints, then the solid features built on it; lengths are millimeters unless a unit is written):

FEATURE [Sketcher::SketchObject] Sketch086
  ArcFitTolerance = 1e-06
  AttachmentSupport = -> [Origin044]
  ExternalTypes = [0]
  FullyConstrained = true
  MakeInternals = false
  MapMode = 5
  sketch-geometry (1):
    g0: Circle CenterX=0 CenterY=0 CenterZ=0 NormalX=0 NormalY=0 NormalZ=1 AngleXU=0 Radius=5.5
  constraints (2):
    c: Diameter(g0) = 11
    c: Coincident(g0,g-1)
FEATURE [PartDesign::Pad] Pad057
  Direction = (0,0,1)
  Length = 2
  Length2 = 10
  Profile = -> Sketch086
  ReferenceAxis = -> Sketch086 [N_Axis]
  Refine = true
  SideType = 0
  Suppressed = false
  Type = 0
  Type2 = 0
FEATURE [Sketcher::SketchObject] Sketch087
  ArcFitTolerance = 1e-06
  AttachmentSupport = -> [Origin044]
  ExternalTypes = [0]
  FullyConstrained = true
  MakeInternals = false
  MapMode = 5
  sketch-geometry (4):
    g0: LineSegment StartX=-3 StartY=3 StartZ=0 EndX=-3 EndY=-3 EndZ=0
    g1: LineSegment StartX=-3 StartY=-3 StartZ=0 EndX=3 EndY=-3 EndZ=0
    g2: LineSegment StartX=3 StartY=-3 StartZ=0 EndX=3 EndY=3 EndZ=0
    g3: LineSegment StartX=3 StartY=3 StartZ=0 EndX=-3 EndY=3 EndZ=0
  constraints (11):
    c: Coincident(g0,g1)
    c: Coincident(g1,g2)
    c: Coincident(g2,g3)
    c: Coincident(g3,g0)
    c: Vertical(g0)
    c: Vertical(g2)
    c: Horizontal(g1)
    c: Horizontal(g3)
    c: Symmetric(g0,g1,g-1)
    c: Equal(g3,g2)
    c: DistanceY(g2,g2) = 6
FEATURE [PartDesign::Pocket] Pocket020
  BaseFeature = -> Pad057
  Direction = (0,0,-1)
  Length = 5
  Length2 = 5
  Profile = -> Sketch087
  ReferenceAxis = -> Sketch087 [N_Axis]
  Refine = true
  Reversed = true
  SideType = 0
  Suppressed = false
  Type = 1
  Type2 = 0
FEATURE [Sketcher::SketchObject] Sketch088
  ArcFitTolerance = 1e-06
  AttachmentSupport = -> [Origin044]
  ExternalGeometry = -> [Pocket020]
  ExternalTypes = [0]
  FullyConstrained = true
  MakeInternals = false
  MapMode = 5
  Placement = pos=(0,0,0) rot=(1,0,0;1.5708rad)
  sketch-geometry (4):
    g0: LineSegment StartX=5.5 StartY=2 StartZ=0 EndX=4.75 EndY=2 EndZ=0
    g1: LineSegment StartX=4.75 StartY=2 StartZ=0 EndX=4.75 EndY=0 EndZ=0
    g2: LineSegment StartX=4.75 StartY=0 StartZ=0 EndX=5.5 EndY=0 EndZ=0
    g3: LineSegment StartX=5.5 StartY=0 StartZ=0 EndX=5.5 EndY=2 EndZ=0
  constraints (11):
    c: Coincident(g0,g1)
    c: Coincident(g1,g2)
    c: Coincident(g2,g3)
    c: Coincident(g3,g0)
    c: Horizontal(g0)
    c: Horizontal(g2)
    c: Vertical(g1)
    c: Vertical(g3)
    c: Coincident(g0,g-3)
    c: PointOnObject(g1,g-1)
    c: Distance(g0,g0) = 0.75
FEATURE [PartDesign::AdditiveHelix] AdditiveHelix001
  Angle = 0
  Axis = (0,2e-16,1)
  Base = (0,0,0)
  BaseFeature = -> Pocket020
  Growth = 2.75
  HasBeenEdited = true
  Height = 0
  LeftHanded = false
  Mode = 3
  Outside = false
  Pitch = 0
  Profile = -> Sketch088
  ReferenceAxis = -> Sketch088 [V_Axis]
  Refine = true
  Suppressed = false
  Tolerance = 0.1
  Turns = 2
FEATURE [Sketcher::SketchObject] Sketch089
  ArcFitTolerance = 1e-06
  AttachmentSupport = -> [Origin044]
  ExternalGeometry = -> [AdditiveHelix001]
  ExternalTypes = [0]
  FullyConstrained = true
  MakeInternals = false
  MapMode = 5
  Placement = pos=(0,0,0) rot=(1,0,0;1.5708rad)
  sketch-geometry (6):
    g0: LineSegment [constr] StartX=5.5 StartY=2 StartZ=0 EndX=-5.5 EndY=2 EndZ=0
    g1: GeomPoint [constr] X=0 Y=2 Z=0
    g2: LineSegment StartX=-5.5 StartY=2 StartZ=0 EndX=-5.5 EndY=0 EndZ=0
    g3: LineSegment StartX=-5.5 StartY=0 StartZ=0 EndX=-4.75 EndY=0 EndZ=0
    g4: LineSegment StartX=-4.75 StartY=0 StartZ=0 EndX=-4.75 EndY=2 EndZ=0
    g5: LineSegment StartX=-4.75 StartY=2 StartZ=0 EndX=-5.5 EndY=2 EndZ=0
  constraints (15):
    c: Coincident(g0,g-3)
    c: Horizontal(g0)
    c: Symmetric(g0,g0,g1)
    c: PointOnObject(g1,g-2)
    c: Coincident(g2,g3)
    c: Coincident(g3,g4)
    c: Coincident(g4,g5)
    c: Coincident(g5,g2)
    c: Vertical(g2)
    c: Vertical(g4)
    c: Horizontal(g3)
    c: Horizontal(g5)
    c: Coincident(g2,g0)
    c: PointOnObject(g3,g-1)
    c: Distance(g5,g5) = 0.75
FEATURE [PartDesign::AdditiveHelix] AdditiveHelix002
  Angle = 0
  Axis = (0,2e-16,1)
  Base = (0,0,0)
  BaseFeature = -> AdditiveHelix001
  Growth = 2.75
  HasBeenEdited = true
  Height = 0
  LeftHanded = false
  Mode = 3
  Outside = false
  Pitch = 0
  Profile = -> Sketch089
  ReferenceAxis = -> Sketch089 [V_Axis]
  Refine = true
  Suppressed = false
  Tolerance = 0.1
  Turns = 2
FEATURE [Sketcher::SketchObject] Sketch090
  ArcFitTolerance = 1e-06
  AttachmentSupport = -> [Origin044]
  ExternalGeometry = -> [AdditiveHelix002]
  ExternalTypes = [0,0]
  FullyConstrained = true
  MakeInternals = false
  MapMode = 5
  sketch-geometry (2):
    g0: Circle CenterX=0 CenterY=0 CenterZ=0 NormalX=0 NormalY=0 NormalZ=1 AngleXU=0 Radius=10.25
    g1: Circle CenterX=0 CenterY=0 CenterZ=0 NormalX=0 NormalY=0 NormalZ=1 AngleXU=0 Radius=11
  constraints (4):
    c: Coincident(g0,g-1)
    c: Diameter(g1) = 22
    c: Coincident(g1,g0)
    c: PointOnObject(g-3,g0)
FEATURE [PartDesign::Pad] Pad058
  BaseFeature = -> AdditiveHelix002
  Direction = (0,0,1)
  Length = 10
  Length2 = 10
  Profile = -> Sketch090
  ReferenceAxis = -> Sketch090 [N_Axis]
  Refine = true
  SideType = 0
  Suppressed = false
  Type = 3
  Type2 = 0
  UpToFace = -> AdditiveHelix002 [Face13]
FEATURE [PartDesign::Fillet] Fillet
  Base = -> Pad058 [Edge46,Edge50,Edge48,Edge45]
  BaseFeature = -> Pad058
  Radius = 2
  Refine = true
  SupportTransform = false
  Suppressed = false
  UseAllEdges = false
FEATURE [PartDesign::Body] Body020  label="spring"
  AllowCompound = false
  Group = -> [Sketch086,Pad057,Sketch087,Pocket020,Sketch088,AdditiveHelix001,Sketch089,AdditiveHelix002,Sketch090,Pad058,Fillet]
  Origin = -> Origin044
  Tip = -> Fillet
COMPONENT P13 — recipe-attached ("shaft", modeled in this document).
Construction recipe (the document's own serialized feature program — sketch geometry with constraints, then the solid features built on it; lengths are millimeters unless a unit is written):

FEATURE [PartDesign::SubShapeBinder] Binder020
  BindCopyOnChange = 0
  BindMode = 0
  ClaimChildren = false
  Context = -> Body021 [Binder020.]
  Fuse = false
  MakeFace = true
  OffsetFill = false
  OffsetIntersection = false
  OffsetJoinType = 0
  OffsetOpenResult = false
  PartialLoad = false
  Refine = true
  Relative = true
  Support = -> [Body020]
  _Version = 2
FEATURE [Sketcher::SketchObject] Sketch091
  ArcFitTolerance = 1e-06
  AttachmentSupport = -> [Origin046]
  ExternalGeometry = -> [Binder020]
  ExternalTypes = [0,0,0,0,0,0,0,0]
  FullyConstrained = true
  MakeInternals = false
  MapMode = 5
  sketch-geometry (8):
    g0: ArcOfCircle CenterX=-1 CenterY=-1 CenterZ=0 NormalX=0 NormalY=0 NormalZ=1 AngleXU=-1.5708 Radius=1.9 StartAngle=4.71239 EndAngle=6.28319
    g1: LineSegment StartX=1 StartY=-2.9 StartZ=0 EndX=-1 EndY=-2.9 EndZ=0
    g2: ArcOfCircle CenterX=1 CenterY=-1 CenterZ=0 NormalX=0 NormalY=0 NormalZ=1 AngleXU=-1.5708 Radius=1.9 StartAngle=0 EndAngle=1.5708
    g3: LineSegment StartX=2.9 StartY=1 StartZ=0 EndX=2.9 EndY=-1 EndZ=0
    g4: ArcOfCircle CenterX=1 CenterY=1 CenterZ=0 NormalX=0 NormalY=0 NormalZ=1 AngleXU=-1.5708 Radius=1.9 StartAngle=1.5708 EndAngle=3.14159
    g5: LineSegment StartX=-1 StartY=2.9 StartZ=0 EndX=1 EndY=2.9 EndZ=0
    g6: ArcOfCircle CenterX=-1 CenterY=1 CenterZ=0 NormalX=0 NormalY=0 NormalZ=1 AngleXU=-1.5708 Radius=1.9 StartAngle=3.14159 EndAngle=4.71239
    g7: LineSegment StartX=-2.9 StartY=-1 StartZ=0 EndX=-2.9 EndY=1 EndZ=0
  constraints (16):
    c: Tangent(g0,g1) = 1.5708
    c: Tangent(g0,g7) = 1.5708
    c: Tangent(g1,g2) = 1.5708
    c: Tangent(g2,g3) = 1.5708
    c: Tangent(g3,g4) = 1.5708
    c: Tangent(g4,g5) = 1.5708
    c: Tangent(g5,g6) = 1.5708
    c: Tangent(g6,g7) = 1.5708
    c: Coincident(g6,g-4)
    c: Coincident(g4,g-6)
    c: Coincident(g2,g-8)
    c: Coincident(g0,g-10)
    c: Horizontal(g5)
    c: Vertical(g7)
    c: Vertical(g3)
    c: Distance(g-7,g3) = 0.1
FEATURE [PartDesign::Pad] Pad059
  Direction = (0,0,1)
  Length = 4
  Length2 = 10
  Profile = -> Sketch091
  ReferenceAxis = -> Sketch091 [N_Axis]
  Refine = true
  SideType = 0
  Suppressed = false
  Type = 0
  Type2 = 0
FEATURE [Sketcher::SketchObject] Sketch092
  ArcFitTolerance = 1e-06
  AttachmentSupport = -> [Pad059]
  ExternalTypes = [0]
  FullyConstrained = true
  MakeInternals = false
  MapMode = 5
  Placement = pos=(0,0,4) rot=(0,0,1;0rad)
  sketch-geometry (7):
    g0: LineSegment StartX=-10 StartY=2.9 StartZ=0 EndX=-10 EndY=-2.9 EndZ=0
    g1: LineSegment StartX=-10 StartY=-2.9 StartZ=0 EndX=10 EndY=-2.9 EndZ=0
    g2: LineSegment StartX=10 StartY=-2.9 StartZ=0 EndX=10 EndY=2.9 EndZ=0
    g3: LineSegment StartX=10 StartY=2.9 StartZ=0 EndX=-10 EndY=2.9 EndZ=0
    g4: GeomPoint X=-10 Y=0 Z=0
    g5: GeomPoint X=0 Y=2.9 Z=0
    g6: LineSegment [constr] StartX=0 StartY=2.9 StartZ=0 EndX=0 EndY=-2.9 EndZ=0
  constraints (16):
    c: Coincident(g0,g1)
    c: Coincident(g1,g2)
    c: Coincident(g2,g3)
    c: Coincident(g3,g0)
    c: Vertical(g0)
    c: Vertical(g2)
    c: Horizontal(g1)
    c: Horizontal(g3)
    c: Symmetric(g0,g0,g4)
    c: PointOnObject(g4,g-1)
    c: Symmetric(g3,g3,g5)
    c: Coincident(g6,g5)
    c: Symmetric(g1,g1,g6)
    c: PointOnObject(g-1,g6)
    c: Distance(g3,g3) = 20
    c: PointOnObject(g-3,g3)
FEATURE [PartDesign::Pad] Pad060
  BaseFeature = -> Pad059
  Direction = (0,0,1)
  Length = 3
  Length2 = 10
  Profile = -> Sketch092
  ReferenceAxis = -> Sketch092 [N_Axis]
  Refine = true
  SideType = 0
  Suppressed = false
  Type = 0
  Type2 = 0
FEATURE [Sketcher::SketchObject] Sketch093
  ArcFitTolerance = 1e-06
  AttachmentSupport = -> [Pad060]
  ExternalGeometry = -> [Pad060]
  ExternalTypes = [0]
  FullyConstrained = true
  MakeInternals = false
  MapMode = 5
  Placement = pos=(0,0,7) rot=(0,0,1;0rad)
  sketch-geometry (4):
    g0: LineSegment [constr] StartX=0 StartY=-2.9 StartZ=0 EndX=0 EndY=2.9 EndZ=0
    g1: LineSegment [constr] StartX=0 StartY=0 StartZ=0 EndX=-10 EndY=0 EndZ=0
    g2: LineSegment [constr] StartX=0 StartY=0 StartZ=0 EndX=10 EndY=0 EndZ=0
    g3: Circle CenterX=-7 CenterY=0 CenterZ=0 NormalX=0 NormalY=0 NormalZ=1 AngleXU=0 Radius=2
  constraints (9):
    c: Symmetric(g-4,g-4,g0)
    c: Symmetric(g-6,g-6,g0)
    c: Coincident(g1,g-1)
    c: Symmetric(g-3,g-3,g1)
    c: Coincident(g2,g1)
    c: Symmetric(g-5,g-5,g2)
    c: Diameter(g3) = 4
    c: PointOnObject(g3,g1)
    c: Distance(g1,g3) = 1
FEATURE [PartDesign::Pocket] Pocket021
  BaseFeature = -> Pad060
  Direction = (0,0,-1)
  Length = 3
  Length2 = 5
  Profile = -> Sketch093
  ReferenceAxis = -> Sketch093 [N_Axis]
  Refine = true
  SideType = 0
  Suppressed = false
  Type = 0
  Type2 = 0
FEATURE [PartDesign::Mirrored] Mirrored002
  BaseFeature = -> Pocket021
  MirrorPlane = -> Sketch093 [V_Axis]
  Originals = -> [Pocket021]
  Refine = true
  Suppressed = false
  TransformMode = 0
FEATURE [PartDesign::Fillet] Fillet010
  Base = -> Mirrored002 [Edge32,Edge38,Edge12,Edge10]
  BaseFeature = -> Mirrored002
  Radius = 2
  Refine = true
  SupportTransform = false
  Suppressed = false
  UseAllEdges = false
FEATURE [PartDesign::Body] Body021  label="shaft"
  AllowCompound = false
  Group = -> [Binder020,Sketch091,Pad059,Sketch092,Pad060,Sketch093,Pocket021,Mirrored002,Fillet010]
  Origin = -> Origin046
  Tip = -> Fillet010
COMPONENT P14 — recipe-attached ("coil", modeled in this document).
Construction recipe (the document's own serialized feature program — sketch geometry with constraints, then the solid features built on it; lengths are millimeters unless a unit is written):

FEATURE [PartDesign::SubShapeBinder] Binder021
  BindCopyOnChange = 0
  BindMode = 0
  ClaimChildren = false
  Context = -> Body022 [Binder021.]
  Fuse = false
  MakeFace = true
  OffsetFill = false
  OffsetIntersection = false
  OffsetJoinType = 0
  OffsetOpenResult = false
  PartialLoad = false
  Refine = true
  Relative = true
  Support = -> [Body021]
  _Version = 2
FEATURE [Sketcher::SketchObject] Sketch094
  ArcFitTolerance = 1e-06
  AttachmentOffset = pos=(0,0,0) rot=(1,0,0;3.14159rad)
  AttachmentSupport = -> [Binder021]
  ExternalGeometry = -> [Binder021]
  ExternalTypes = [0]
  FullyConstrained = true
  MakeInternals = false
  MapMode = 5
  Placement = pos=(0,0,4) rot=(0,0,1;0rad)
  sketch-geometry (2):
    g0: ArcOfCircle CenterX=-7 CenterY=-4e-16 CenterZ=0 NormalX=0 NormalY=0 NormalZ=1 AngleXU=0 Radius=2 StartAngle=1.5708 EndAngle=4.71239
    g1: LineSegment StartX=-7 StartY=-2 StartZ=0 EndX=-7 EndY=2 EndZ=0
  constraints (6):
    c: Angle(g0) = 3.14159
    c: Coincident(g0,g-3)
    c: PointOnObject(g0,g-3)
    c: Coincident(g1,g0)
    c: Coincident(g1,g0)
    c: Vertical(g1)
FEATURE [PartDesign::Pad] Pad061
  Direction = (0,1e-16,1)
  Length = 10
  Length2 = 10
  Profile = -> Sketch094
  ReferenceAxis = -> Sketch094 [N_Axis]
  Refine = true
  SideType = 0
  Suppressed = false
  Type = 3
  Type2 = 0
  UpToFace = -> Binder021 [Face5]
FEATURE [Sketcher::SketchObject] Sketch095
  ArcFitTolerance = 1e-06
  AttachmentSupport = -> [Pad061]
  ExternalTypes = [0]
  FullyConstrained = true
  MakeInternals = false
  MapMode = 5
  Placement = pos=(0,0,7) rot=(0,0,1;0rad)
  sketch-geometry (7):
    g0: LineSegment StartX=-9 StartY=2 StartZ=0 EndX=-9 EndY=-2 EndZ=0
    g1: LineSegment StartX=-9 StartY=-2 StartZ=0 EndX=-7 EndY=-2 EndZ=0
    g2: LineSegment StartX=-7 StartY=-2 StartZ=0 EndX=-7 EndY=2 EndZ=0
    g3: LineSegment StartX=-7 StartY=2 StartZ=0 EndX=-9 EndY=2 EndZ=0
    g4: LineSegment [constr] StartX=-7 StartY=0 StartZ=0 EndX=-9 EndY=0 EndZ=0
    g5: LineSegment [constr] StartX=-7 StartY=0 StartZ=0 EndX=-7 EndY=-2 EndZ=0
    g6: LineSegment [constr] StartX=-7 StartY=0 StartZ=0 EndX=-7 EndY=2 EndZ=0
  constraints (21):
    c: Coincident(g0,g1)
    c: Coincident(g1,g2)
    c: Coincident(g2,g3)
    c: Coincident(g3,g0)
    c: Vertical(g0)
    c: Vertical(g2)
    c: Horizontal(g1)
    c: Horizontal(g3)
    c: Coincident(g4,g-3)
    c: PointOnObject(g4,g-3)
    c: Horizontal(g4)
    c: PointOnObject(g4,g0)
    c: Coincident(g5,g4)
    c: PointOnObject(g5,g-3)
    c: Vertical(g5)
    c: Coincident(g6,g4)
    c: PointOnObject(g6,g-3)
    c: Vertical(g6)
    c: PointOnObject(g6,g3)
    c: PointOnObject(g5,g1)
    c: Distance(g3,g3) = 2
FEATURE [PartDesign::Pad] Pad062
  BaseFeature = -> Pad061
  Direction = (0,0,1)
  Length = 20
  Length2 = 10
  Profile = -> Sketch095
  ReferenceAxis = -> Sketch095 [N_Axis]
  Refine = true
  SideType = 0
  Suppressed = false
  Type = 0
  Type2 = 0
FEATURE [Sketcher::SketchObject] Sketch096
  ArcFitTolerance = 1e-06
  AttachmentSupport = -> [Pad062]
  ExternalGeometry = -> [Pad062]
  ExternalTypes = [0,0,0]
  FullyConstrained = true
  MakeInternals = false
  MapMode = 5
  Placement = pos=(-7,0,0) rot=(0.57735,0.57735,0.57735;2.0944rad)
  sketch-geometry (7):
    g0: GeomPoint X=1e-16 Y=17 Z=0
    g1: LineSegment [constr] StartX=-2 StartY=17 StartZ=0 EndX=2 EndY=17 EndZ=0
    g2: GeomPoint [constr] X=1e-16 Y=17 Z=0
    g3: LineSegment [constr] StartX=0 StartY=27 StartZ=0 EndX=1e-16 EndY=17 EndZ=0
    g4: LineSegment [constr] StartX=1e-16 StartY=17 StartZ=0 EndX=-1.17e-14 EndY=7 EndZ=0
    g5: Circle CenterX=0 CenterY=22.5 CenterZ=0 NormalX=0 NormalY=0 NormalZ=1 AngleXU=0 Radius=1.5
    g6: Circle CenterX=-6.4e-15 CenterY=11.5 CenterZ=0 NormalX=0 NormalY=0 NormalZ=1 AngleXU=0 Radius=1.5
  constraints (14):
    c: Symmetric(g-5,g-5,g1)
    c: Symmetric(g-6,g-6,g1)
    c: Symmetric(g1,g1,g2)
    c: Coincident(g0,g2)
    c: Symmetric(g-4,g-4,g3)
    c: Coincident(g3,g2)
    c: Coincident(g4,g2)
    c: Symmetric(g-3,g-3,g4)
    c: Diameter(g5) = 3
    c: PointOnObject(g5,g3)
    c: Distance(g3,g5) = 3
    c: Diameter(g6) = 3
    c: PointOnObject(g6,g4)
    c: Distance(g4,g6) = 3
FEATURE [PartDesign::Pad] Pad063
  BaseFeature = -> Pad062
  Direction = (1,0,0)
  Length = 9
  Length2 = 10
  Profile = -> Sketch096
  ReferenceAxis = -> Sketch096 [N_Axis]
  Refine = true
  SideType = 0
  Suppressed = false
  Type = 0
  Type2 = 0
FEATURE [Part::DatumPlane] DatumPlane
  AttachmentOffset = pos=(0,0,0) rot=(-0.57735,0.57735,0.57735;2.0944rad)
  AttachmentSupport = -> [Sketch096]
  MapMode = 1
  Placement = pos=(-7,0,17) rot=(0,0,1;3.14159rad)
FEATURE [PartDesign::Mirrored] Mirror006
  MirrorPlane = -> YZ_Plane023
  Refine = true
  Suppressed = false
  TransformMode = 0
FEATURE [PartDesign::Mirrored] Mirror007
  MirrorPlane = -> DatumPlane
  Refine = true
  Suppressed = false
  TransformMode = 0
FEATURE [PartDesign::MultiTransform] MultiTransform003
  BaseFeature = -> Pad063
  Originals = -> [Pad063,Pad062,Pad061]
  Refine = true
  Suppressed = false
  TransformMode = 0
  Transformations = -> [Mirror006,Mirror007]
FEATURE [PartDesign::Body] Body022  label="coil"
  AllowCompound = false
  Group = -> [Binder021,Sketch094,Pad061,Sketch095,Pad062,Sketch096,Pad063,DatumPlane,MultiTransform003,Mirror006,Mirror007]
  Origin = -> Origin048
  Tip = -> MultiTransform003
COMPONENT P15 — recipe-attached ("design4-rotor", modeled in this document).
Construction recipe (the document's own serialized feature program — sketch geometry with constraints, then the solid features built on it; lengths are millimeters unless a unit is written):

FEATURE [PartDesign::SubShapeBinder] Binder025
  BindCopyOnChange = 0
  BindMode = 0
  ClaimChildren = false
  Context = -> Body023 [Binder025.]
  Fuse = false
  MakeFace = true
  OffsetFill = false
  OffsetIntersection = false
  OffsetJoinType = 0
  OffsetOpenResult = false
  PartialLoad = false
  Refine = true
  Relative = true
  Support = -> [Body002]
  _Version = 2
FEATURE [Sketcher::SketchObject] Sketch
  ArcFitTolerance = 1e-06
  AttachmentSupport = -> [Origin053]
  ExternalGeometry = -> [Binder025]
  ExternalTypes = [0,0]
  FullyConstrained = true
  MakeInternals = false
  MapMode = 5
FEATURE [PartDesign::Pad] Pad067
  Direction = (0,0,1)
  Length = 10
  Length2 = 10
  Offset = -2
  Profile = -> Sketch
  ReferenceAxis = -> Sketch [N_Axis]
  Refine = true
  SideType = 0
  Suppressed = false
  Type = 3
  Type2 = 0
  UpToFace = -> Binder025 [Face4]
FEATURE [Sketcher::SketchObject] Sketch108
  ArcFitTolerance = 1e-06
  AttachmentSupport = -> [Pad067]
  ExternalGeometry = -> [Pad067]
  ExternalTypes = [0]
  FullyConstrained = true
  MakeInternals = false
  MapMode = 5
  Placement = pos=(0,0,10) rot=(0,0,1;0rad)
  expr: Constraints[2] = VarSet.big_magnet_diameter
  sketch-geometry (3):
    g0: Circle CenterX=0 CenterY=0 CenterZ=0 NormalX=0 NormalY=0 NormalZ=1 AngleXU=0 Radius=8.3
    g1: LineSegment [constr] StartX=-6.3 StartY=0 StartZ=0 EndX=6.3 EndY=0 EndZ=0
    g2: GeomPoint X=0 Y=0 Z=0
  constraints (6):
    c: Coincident(g0,g-3)
    c: Horizontal(g1)
    c: Distance(g1,g1) = 12.6
    c: Symmetric(g1,g1,g2)
    c: Coincident(g0,g2)
    c: Distance(g1,g0) = 2
FEATURE [PartDesign::Pad] Pad068
  BaseFeature = -> Pad067
  Direction = (0,0,1)
  Length = 2
  Length2 = 10
  Profile = -> Sketch108
  ReferenceAxis = -> Sketch108 [N_Axis]
  Refine = true
  SideType = 0
  Suppressed = false
  Type = 0
  Type2 = 0
FEATURE [Sketcher::SketchObject] Sketch109
  ArcFitTolerance = 1e-06
  AttachmentSupport = -> [Pad068]
  ExternalGeometry = -> [Pad068]
  ExternalTypes = [0]
  FullyConstrained = true
  MakeInternals = false
  MapMode = 5
  Placement = pos=(0,0,12) rot=(0,0,1;0rad)
  sketch-geometry (1):
    g0: Circle CenterX=0 CenterY=0 CenterZ=0 NormalX=0 NormalY=0 NormalZ=1 AngleXU=0 Radius=8.3
  constraints (2):
    c: Coincident(g0,g-3)
    c: Tangent(g0,g-3)
FEATURE [PartDesign::Pad] Pad069
  BaseFeature = -> Pad068
  Direction = (0,0,1)
  Length = 25.2
  Length2 = 10
  Profile = -> Sketch109
  ReferenceAxis = -> Sketch109 [N_Axis]
  Refine = true
  SideType = 0
  Suppressed = false
  Type = 0
  Type2 = 0
  expr: Length = 2 * VarSet.big_magnet_diameter
FEATURE [PartDesign::SubShapeBinder] Binder028
  BindCopyOnChange = 0
  BindMode = 0
  ClaimChildren = false
  Context = -> Body023 [Binder028.]
  Fuse = false
  MakeFace = true
  OffsetFill = false
  OffsetIntersection = false
  OffsetJoinType = 0
  OffsetOpenResult = false
  PartialLoad = false
  Refine = true
  Relative = true
  Support = -> [Pad068]
  _Version = 2
FEATURE [Sketcher::SketchObject] Sketch113
  ArcFitTolerance = 1e-06
  AttachmentSupport = -> [Pad069]
  ExternalTypes = [0]
  FullyConstrained = true
  MakeInternals = false
  MapMode = 5
  Placement = pos=(0,0,37.2) rot=(0,0,1;0rad)
  expr: Constraints[8] = VarSet.big_magnet_diameter + 0.4 mm
  expr: Constraints[9] = VarSet.big_magnet_height + 0.4 mm
  sketch-geometry (5):
    g0: LineSegment StartX=-3.35 StartY=-6.5 StartZ=0 EndX=3.35 EndY=-6.5 EndZ=0
    g1: LineSegment StartX=3.35 StartY=-6.5 StartZ=0 EndX=3.35 EndY=6.5 EndZ=0
    g2: LineSegment StartX=3.35 StartY=6.5 StartZ=0 EndX=-3.35 EndY=6.5 EndZ=0
    g3: LineSegment StartX=-3.35 StartY=6.5 StartZ=0 EndX=-3.35 EndY=-6.5 EndZ=0
    g4: GeomPoint [constr] X=0 Y=0 Z=0
  constraints (11):
    c: Coincident(g0,g1)
    c: Coincident(g1,g2)
    c: Coincident(g2,g3)
    c: Coincident(g3,g0)
    c: Horizontal(g0)
    c: Vertical(g1)
    c: Symmetric(g2,g0,g4)
    c: Coincident(g4,g-1)
    c: DistanceY(g1,g1) = 13
    c: Distance(g2,g2) = 6.7
    c: Symmetric(g2,g0,g4)
FEATURE [PartDesign::Pocket] Pocket025
  BaseFeature = -> Pad069
  Direction = (0,0,-1)
  Length = 5
  Length2 = 5
  Profile = -> Sketch113
  ReferenceAxis = -> Sketch113 [N_Axis]
  Refine = true
  SideType = 0
  Suppressed = false
  Type = 3
  Type2 = 0
  UpToFace = -> Binder028 [Face5]
FEATURE [PartDesign::Body] Body023  label="design4-rotor"
  AllowCompound = false
  Group = -> [Binder025,Sketch,Pad067,Sketch108,Pad068,Sketch109,Pad069,Binder028,Sketch113,Pocket025]
  Origin = -> Origin053
  Tip = -> Pocket025
COMPONENT P16 — recipe-attached ("design4-stator", modeled in this document).
Construction recipe (the document's own serialized feature program — sketch geometry with constraints, then the solid features built on it; lengths are millimeters unless a unit is written):

FEATURE [PartDesign::SubShapeBinder] Binder026
  BindCopyOnChange = 0
  BindMode = 0
  ClaimChildren = false
  Context = -> Body024 [Binder026.]
  Fuse = false
  MakeFace = true
  OffsetFill = false
  OffsetIntersection = false
  OffsetJoinType = 0
  OffsetOpenResult = false
  PartialLoad = false
  Refine = true
  Relative = true
  Support = -> [Body002]
  _Version = 2
FEATURE [Sketcher::SketchObject] Sketch107
  ArcFitTolerance = 1e-06
  AttachmentSupport = -> [Origin055]
  ExternalGeometry = -> [Binder026]
  ExternalTypes = [0,0]
  FullyConstrained = true
  MakeInternals = false
  MapMode = 5
  sketch-geometry (2):
    g0: Circle CenterX=0 CenterY=0 CenterZ=0 NormalX=0 NormalY=0 NormalZ=1 AngleXU=0 Radius=13
    g1: Circle CenterX=0 CenterY=0 CenterZ=0 NormalX=0 NormalY=0 NormalZ=1 AngleXU=0 Radius=15
  constraints (4):
    c: Coincident(g0,g-4)
    c: Equal(g0,g-4)
    c: Coincident(g1,g0)
    c: Distance(g0,g1) = 2
FEATURE [PartDesign::Pad] Pad066
  Direction = (0,0,1)
  Length = 4
  Length2 = 10
  Profile = -> Sketch107
  ReferenceAxis = -> Sketch107 [N_Axis]
  Refine = true
  SideType = 0
  Suppressed = false
  Type = 3
  Type2 = 0
  UpToFace = -> Binder026 [Face4]
FEATURE [PartDesign::SubShapeBinder] Binder027
  BindCopyOnChange = 0
  BindMode = 0
  ClaimChildren = false
  Context = -> Body024 [Binder027.]
  Fuse = false
  MakeFace = true
  OffsetFill = false
  OffsetIntersection = false
  OffsetJoinType = 0
  OffsetOpenResult = false
  PartialLoad = false
  Refine = true
  Relative = true
  Support = -> [Body023]
  _Version = 2
FEATURE [Sketcher::SketchObject] Sketch111
  ArcFitTolerance = 1e-06
  AttachmentSupport = -> [Pad066]
  ExternalGeometry = -> [Pad066,Binder027]
  ExternalTypes = [0,0]
  FullyConstrained = true
  MakeInternals = false
  MapMode = 5
  Placement = pos=(0,0,8) rot=(0,0,1;0rad)
  sketch-geometry (2):
    g0: Circle CenterX=0 CenterY=0 CenterZ=0 NormalX=0 NormalY=0 NormalZ=1 AngleXU=0 Radius=10.3
    g1: Circle CenterX=0 CenterY=0 CenterZ=0 NormalX=0 NormalY=0 NormalZ=1 AngleXU=0 Radius=15
  constraints (4):
    c: Coincident(g0,g-3)
    c: Coincident(g1,g0)
    c: Tangent(g1,g-3)
    c: Distance(g-4,g0) = 2
FEATURE [PartDesign::Pad] Pad071
  BaseFeature = -> Pad066
  Direction = (0,0,1)
  Length = 2
  Length2 = 10
  Profile = -> Sketch111
  ReferenceAxis = -> Sketch111 [N_Axis]
  Refine = true
  SideType = 0
  Suppressed = false
  Type = 0
  Type2 = 0
FEATURE [Sketcher::SketchObject] Sketch112
  ArcFitTolerance = 1e-06
  AttachmentSupport = -> [Pad071]
  ExternalGeometry = -> [Pad071]
  ExternalTypes = [0,0]
  FullyConstrained = true
  MakeInternals = false
  MapMode = 5
  Placement = pos=(0,0,10) rot=(0,0,1;0rad)
  sketch-geometry (1):
    g0: Circle CenterX=0 CenterY=0 CenterZ=0 NormalX=0 NormalY=0 NormalZ=1 AngleXU=0 Radius=13.8
  constraints (2):
    c: Coincident(g0,g-3)
    c: Distance(g0,g-3) = 3.5
FEATURE [PartDesign::Pad] Pad072
  BaseFeature = -> Pad071
  Direction = (0,0,1)
  Length = 10
  Length2 = 10
  Profile = -> Sketch112
  ReferenceAxis = -> Sketch112 [N_Axis]
  Refine = true
  SideType = 0
  Suppressed = false
  Type = 3
  Type2 = 0
  UpToFace = -> Pocket025 [Face1]
FEATURE [PartDesign::Body] Body024  label="design4-stator"
  AllowCompound = false
  Group = -> [Binder027,Binder026,Sketch107,Pad066,Sketch111,Pad071,Sketch112,Pad072]
  Origin = -> Origin055
  Tip = -> Pad072
COMPONENT P17 — recipe-attached ("design5-stator", modeled in this document).
Construction recipe (the document's own serialized feature program — sketch geometry with constraints, then the solid features built on it; lengths are millimeters unless a unit is written):

FEATURE [PartDesign::SubShapeBinder] Binder030
  BindCopyOnChange = 0
  BindMode = 0
  ClaimChildren = false
  Context = -> Body025 [Binder030.]
  Fuse = false
  MakeFace = true
  OffsetFill = false
  OffsetIntersection = false
  OffsetJoinType = 0
  OffsetOpenResult = false
  PartialLoad = false
  Refine = true
  Relative = true
  Support = -> [Body026]
  _Version = 2
FEATURE [PartDesign::SubShapeBinder] Binder031
  BindCopyOnChange = 0
  BindMode = 0
  ClaimChildren = false
  Context = -> Body025 [Binder031.]
  Fuse = false
  MakeFace = true
  OffsetFill = false
  OffsetIntersection = false
  OffsetJoinType = 0
  OffsetOpenResult = false
  PartialLoad = false
  Refine = true
  Relative = true
  Support = -> [Body002]
  _Version = 2
FEATURE [Sketcher::SketchObject] Sketch118
  ArcFitTolerance = 1e-06
  AttachmentSupport = -> [Origin057]
  ExternalGeometry = -> [Binder031]
  ExternalTypes = [0]
  FullyConstrained = true
  MakeInternals = false
  MapMode = 5
  sketch-geometry (1):
    g0: Circle CenterX=0 CenterY=0 CenterZ=0 NormalX=0 NormalY=0 NormalZ=1 AngleXU=0 Radius=15.5
  constraints (2):
    c: Coincident(g0,g-3)
    c: Distance(g-3,g0) = 2.5
FEATURE [PartDesign::Pad] Pad075
  Direction = (0,0,1)
  Length = 10
  Length2 = 10
  Profile = -> Sketch118
  ReferenceAxis = -> Sketch118 [N_Axis]
  Refine = true
  SideType = 0
  Suppressed = false
  Type = 3
  Type2 = 0
  UpToFace = -> Binder031 [Face4]
FEATURE [Sketcher::SketchObject] Sketch119
  ArcFitTolerance = 1e-06
  AttachmentSupport = -> [Pad075]
  ExternalGeometry = -> [Pad075,Binder031]
  ExternalTypes = [0,0]
  FullyConstrained = true
  MakeInternals = false
  MapMode = 5
  Placement = pos=(0,0,8) rot=(0,0,1;0rad)
  sketch-geometry (1):
    g0: Circle CenterX=0 CenterY=0 CenterZ=0 NormalX=0 NormalY=0 NormalZ=1 AngleXU=0 Radius=11
  constraints (2):
    c: Coincident(g0,g-1)
    c: Distance(g-4,g0) = 6
FEATURE [PartDesign::Pad] Pad076
  BaseFeature = -> Pad075
  Direction = (0,0,1)
  Length = 2
  Length2 = 10
  Profile = -> Sketch119
  ReferenceAxis = -> Sketch119 [N_Axis]
  Refine = true
  SideType = 0
  Suppressed = false
  Type = 0
  Type2 = 0
FEATURE [PartDesign::Body] Body025  label="design5-stator"
  AllowCompound = false
  Group = -> [Binder030,Binder031,Sketch118,Pad075,Sketch119,Pad076]
  Origin = -> Origin057
  Tip = -> Pad076
COMPONENT P18 — recipe-attached ("design5-rotor", modeled in this document).
Construction recipe (the document's own serialized feature program — sketch geometry with constraints, then the solid features built on it; lengths are millimeters unless a unit is written):

FEATURE [PartDesign::SubShapeBinder] Binder029
  BindCopyOnChange = 0
  BindMode = 0
  ClaimChildren = false
  Context = -> Body026 [Binder029.]
  Fuse = false
  MakeFace = true
  OffsetFill = false
  OffsetIntersection = false
  OffsetJoinType = 0
  OffsetOpenResult = false
  PartialLoad = false
  Refine = true
  Relative = true
  Support = -> [Body002]
  _Version = 2
FEATURE [Sketcher::SketchObject] Sketch114
  ArcFitTolerance = 1e-06
  AttachmentSupport = -> [Origin059]
  ExternalGeometry = -> [Binder029]
  ExternalTypes = [0]
  FullyConstrained = true
  MakeInternals = false
  MapMode = 5
FEATURE [PartDesign::Pad] Pad073
  Direction = (0,0,1)
  Length = 10
  Length2 = 10
  Profile = -> Sketch114
  ReferenceAxis = -> Sketch114 [N_Axis]
  Refine = true
  SideType = 0
  Suppressed = false
  Type = 3
  Type2 = 0
  UpToFace = -> Binder029 [Face4]
FEATURE [Sketcher::SketchObject] Sketch115
  ArcFitTolerance = 1e-06
  AttachmentSupport = -> [Pad073]
  ExternalGeometry = -> [Pad073]
  ExternalTypes = [0]
  FullyConstrained = true
  MakeInternals = false
  MapMode = 5
  Placement = pos=(0,0,8) rot=(0,0,1;0rad)
  expr: Constraints[17] = VarSet.magnet_height + 0.2 mm
  expr: Constraints[18] = VarSet.magnet_diameter + 4 mm
  sketch-geometry (13):
    g0: LineSegment [constr] StartX=3.9 StartY=5.2 StartZ=0 EndX=0.5 EndY=5.2 EndZ=0
    g1: LineSegment [constr] StartX=0.5 StartY=5.2 StartZ=0 EndX=0.5 EndY=-5.2 EndZ=0
    g2: LineSegment [constr] StartX=0.5 StartY=-5.2 StartZ=0 EndX=3.9 EndY=-5.2 EndZ=0
    g3: LineSegment [constr] StartX=3.9 StartY=-5.2 StartZ=0 EndX=3.9 EndY=5.2 EndZ=0
    g4: LineSegment [constr] StartX=0.5 StartY=0 StartZ=0 EndX=0 EndY=0 EndZ=0
    g5: LineSegment [constr] StartX=0.5 StartY=5.2 StartZ=0 EndX=3.9 EndY=-5.2 EndZ=0
    g6: GeomPoint [constr] X=2.2 Y=0 Z=0
    g7: LineSegment StartX=3.9 StartY=-5.2 StartZ=0 EndX=3.9 EndY=5.2 EndZ=0
    g8: LineSegment StartX=3.9 StartY=5.2 StartZ=0 EndX=-3.9 EndY=5.2 EndZ=0
    g9: LineSegment StartX=-3.9 StartY=5.2 StartZ=0 EndX=-3.9 EndY=-5.2 EndZ=0
    g10: LineSegment StartX=-3.9 StartY=-5.2 StartZ=0 EndX=3.9 EndY=-5.2 EndZ=0
    g11: LineSegment [constr] StartX=3.9 StartY=5.2 StartZ=0 EndX=0 EndY=5.2 EndZ=0
    g12: LineSegment [constr] StartX=0 StartY=5.2 StartZ=0 EndX=-3.9 EndY=5.2 EndZ=0
  constraints (34):
    c: Coincident(g0,g1)
    c: Coincident(g1,g2)
    c: Coincident(g2,g3)
    c: Coincident(g3,g0)
    c: Horizontal(g0)
    c: Horizontal(g2)
    c: Vertical(g1)
    c: Vertical(g3)
    c: PointOnObject(g4,g1)
    c: PointOnObject(g4,g-2)
    c: Distance(g4,g4) = 0.5
    c: Horizontal(g4)
    c: PointOnObject(g4,g-1)
    c: Coincident(g5,g0)
    c: Coincident(g5,g2)
    c: Symmetric(g5,g5,g6)
    c: PointOnObject(g6,g-1)
    c: Distance(g0,g0) = 3.4
    c: DistanceY(g3,g3) = 10.4
    c: Coincident(g7,g8)
    c: Coincident(g8,g9)
    c: Coincident(g9,g10)
    c: Coincident(g10,g7)
    c: Vertical(g9)
    c: Horizontal(g8)
    c: Horizontal(g10)
    c: Coincident(g7,g2)
    c: Coincident(g7,g0)
    c: Coincident(g11,g0)
    c: PointOnObject(g11,g-2)
    c: Coincident(g12,g11)
    c: Coincident(g12,g8)
    c: Equal(g12,g11)
    c: PointOnObject(g11,g8)
FEATURE [PartDesign::Pad] Pad074
  BaseFeature = -> Pad073
  Direction = (0,0,1)
  Length = 22.8
  Length2 = 10
  Profile = -> Sketch115
  ReferenceAxis = -> Sketch115 [N_Axis]
  Refine = true
  SideType = 0
  Suppressed = false
  Type = 0
  Type2 = 0
  expr: Length = 10 mm + 2 * VarSet.magnet_diameter
FEATURE [Sketcher::SketchObject] Sketch116
  ArcFitTolerance = 1e-06
  AttachmentSupport = -> [Pad074]
  ExternalGeometry = -> [Pad074,Binder029]
  ExternalTypes = [0,0,0,0]
  FullyConstrained = true
  MakeInternals = false
  MapMode = 5
  Placement = pos=(3.9,0,0) rot=(0.57735,0.57735,0.57735;2.0944rad)
  expr: Constraints[0] = VarSet.magnet_diameter + 0.2 mm
  expr: Constraints[1] = VarSet.magnet_diameter + 0.2 mm
  sketch-geometry (9):
    g0: Circle CenterX=0 CenterY=18.9 CenterZ=0 NormalX=0 NormalY=0 NormalZ=1 AngleXU=0 Radius=3.3
    g1: Circle CenterX=-4e-16 CenterY=27 CenterZ=0 NormalX=0 NormalY=0 NormalZ=1 AngleXU=0 Radius=3.3
    g2: GeomPoint X=-4e-16 Y=30.3 Z=0
    g3: LineSegment [constr] StartX=-4e-16 StartY=30.3 StartZ=0 EndX=-4e-16 EndY=30.8 EndZ=0
    g4: GeomPoint [constr] X=-4e-16 Y=30.8 Z=0
    g5: LineSegment [constr] StartX=-4e-16 StartY=27 StartZ=0 EndX=-4e-16 EndY=30.3 EndZ=0
    g6: GeomPoint [constr] X=0 Y=23.7 Z=0
    g7: LineSegment [constr] StartX=0 StartY=23.7 StartZ=0 EndX=0 EndY=22.2 EndZ=0
    g8: LineSegment [constr] StartX=0 StartY=22.2 StartZ=0 EndX=0 EndY=18.9 EndZ=0
  constraints (20):
    c: Diameter(g1) = 6.6
    c: Diameter(g0) = 6.6
    c: PointOnObject(g2,g1)
    c: Coincident(g3,g2)
    c: Vertical(g3)
    c: Distance(g3,g3) = 0.5
    c: Symmetric(g-3,g-3,g4)
    c: Coincident(g4,g3)
    c: Coincident(g5,g1)
    c: Coincident(g5,g2)
    c: Vertical(g5)
    c: PointOnObject(g6,g1)
    c: Coincident(g7,g6)
    c: PointOnObject(g7,g0)
    c: Vertical(g7)
    c: Coincident(g8,g7)
    c: Coincident(g8,g0)
    c: Vertical(g8)
    c: PointOnObject(g0,g-2)
    c: DistanceY(g7,g7) = 1.5
FEATURE [PartDesign::Pocket] Pocket026
  BaseFeature = -> Pad074
  Direction = (-1,0,0)
  Length = 3.2
  Length2 = 5
  Profile = -> Sketch116
  ReferenceAxis = -> Sketch116 [N_Axis]
  Refine = true
  SideType = 0
  Suppressed = false
  Type = 0
  Type2 = 0
  expr: Length = VarSet.magnet_height
FEATURE [PartDesign::Fillet] Fillet012
  Base = -> Pocket026 [Edge19,Edge20]
  BaseFeature = -> Pocket026
  Radius = 0.4
  Refine = true
  SupportTransform = false
  Suppressed = false
  UseAllEdges = false
FEATURE [PartDesign::Mirrored] Mirrored
  BaseFeature = -> Fillet012
  MirrorPlane = -> YZ_Plane027
  Originals = -> [Pocket026,Fillet012]
  Refine = true
  Suppressed = false
  TransformMode = 0
FEATURE [Sketcher::SketchObject] Sketch117
  ArcFitTolerance = 1e-06
  AttachmentSupport = -> [Mirrored]
  ExternalGeometry = -> [Mirrored]
  ExternalTypes = [0,0,0]
  FullyConstrained = true
  MakeInternals = false
  MapMode = 5
  Placement = pos=(0,0,8) rot=(1,0,0;3.14159rad)
  sketch-geometry (8):
    g0: GeomPoint [constr] X=-1e-16 Y=-1e-16 Z=0
    g1: LineSegment StartX=3.9 StartY=-5.2 StartZ=0 EndX=3.9 EndY=5.2 EndZ=0
    g2: LineSegment StartX=-3.9 StartY=5.2 StartZ=0 EndX=-3.9 EndY=-5.2 EndZ=0
    g3: GeomPoint [constr] X=-1e-16 Y=-1e-16 Z=0
    g4: GeomPoint [constr] X=-1e-16 Y=-1e-16 Z=0
    g5: LineSegment StartX=-3.9 StartY=-5.2 StartZ=0 EndX=3.9 EndY=-5.2 EndZ=0
    g6: LineSegment StartX=3.9 StartY=5.2 StartZ=0 EndX=-3.9 EndY=5.2 EndZ=0
    g7: Circle CenterX=-1e-16 CenterY=-1e-16 CenterZ=0 NormalX=0 NormalY=0 NormalZ=1 AngleXU=0 Radius=2
  constraints (13):
    c: Symmetric(g1,g2,g3)
    c: Coincident(g3,g0)
    c: Coincident(g4,g0)
    c: Coincident(g5,g2)
    c: Coincident(g5,g1)
    c: Coincident(g6,g1)
    c: Coincident(g6,g2)
    c: Diameter(g7) = 4
    c: Coincident(g7,g0)
    c: Coincident(g2,g-7)
    c: Coincident(g-7,g1)
    c: Coincident(g2,g-10)
    c: Coincident(g1,g-11)
FEATURE [PartDesign::Pocket] Pocket027
  BaseFeature = -> Mirrored
  Direction = (0,0,1)
  Length = 7.5
  Length2 = 5
  Offset = -16
  Profile = -> Sketch117
  ReferenceAxis = -> Sketch117 [N_Axis]
  Refine = true
  SideType = 0
  Suppressed = false
  Type = 3
  Type2 = 0
  UpToFace = -> Mirrored [Face5]
FEATURE [Sketcher::SketchObject] Sketch124
  ArcFitTolerance = 1e-06
  AttachmentSupport = -> [Pocket027]
  ExternalTypes = [0]
  FullyConstrained = true
  MakeInternals = false
  MapMode = 5
  Placement = pos=(0,0,30.8) rot=(0,0,1;0rad)
FEATURE [PartDesign::Chamfer] Chamfer002
  Angle = 45
  Base = -> Pocket027 [Edge10]
  BaseFeature = -> Pocket027
  ChamferType = 0
  FlipDirection = false
  Refine = true
  Size = 1.9
  Size2 = 1
  SupportTransform = false
  Suppressed = false
  UseAllEdges = false
FEATURE [PartDesign::Fillet] Fillet013
  Base = -> Chamfer002 [Edge12,Edge14,Edge22,Edge28]
  BaseFeature = -> Chamfer002
  Radius = 1
  Refine = true
  SupportTransform = false
  Suppressed = false
  UseAllEdges = false
FEATURE [PartDesign::Body] Body026  label="design5-rotor"
  AllowCompound = false
  Group = -> [Binder029,Sketch114,Pad073,Sketch115,Pad074,Sketch116,Pocket026,Fillet012,Mirrored,Sketch117,Pocket027,Sketch124,Chamfer002,Fillet013]
  Origin = -> Origin059
  Tip = -> Fillet013
COMPONENT P19 — recipe-attached ("design5-coil-holder", modeled in this document).
Construction recipe (the document's own serialized feature program — sketch geometry with constraints, then the solid features built on it; lengths are millimeters unless a unit is written):

FEATURE [PartDesign::SubShapeBinder] Binder032
  BindCopyOnChange = 0
  BindMode = 0
  ClaimChildren = false
  Context = -> Body027 [Binder032.]
  Fuse = false
  MakeFace = true
  OffsetFill = false
  OffsetIntersection = false
  OffsetJoinType = 0
  OffsetOpenResult = false
  PartialLoad = false
  Placement = pos=(0,0,0) rot=(0,0,1;1.5708rad)
  Refine = true
  Relative = true
  Support = -> [Body026]
  _Version = 2
FEATURE [PartDesign::SubShapeBinder] Binder033
  BindCopyOnChange = 0
  BindMode = 0
  ClaimChildren = false
  Context = -> Body027 [Binder033.]
  Fuse = false
  MakeFace = true
  OffsetFill = false
  OffsetIntersection = false
  OffsetJoinType = 0
  OffsetOpenResult = false
  PartialLoad = false
  Refine = true
  Relative = true
  Support = -> [Body025]
  _Version = 2
FEATURE [Sketcher::SketchObject] Sketch120
  ArcFitTolerance = 1e-06
  AttachmentSupport = -> [Binder033]
  ExternalGeometry = -> [Binder033,Binder032]
  ExternalTypes = [0,0]
  FullyConstrained = true
  MakeInternals = false
  MapMode = 5
  Placement = pos=(0,0,8) rot=(1,0,0;3.14159rad)
  sketch-geometry (5):
    g0: GeomPoint [constr] X=-8 Y=0 Z=0
    g1: GeomPoint X=-11 Y=0 Z=0
    g2: LineSegment [constr] StartX=-11 StartY=0 StartZ=0 EndX=-8 EndY=0 EndZ=0
    g3: Circle CenterX=0 CenterY=0 CenterZ=0 NormalX=0 NormalY=0 NormalZ=1 AngleXU=0 Radius=8
    g4: Circle CenterX=0 CenterY=0 CenterZ=0 NormalX=0 NormalY=0 NormalZ=1 AngleXU=0 Radius=10.9
  constraints (10):
    c: PointOnObject(g1,g-1)
    c: Coincident(g3,g-4)
    c: PointOnObject(g0,g3)
    c: Coincident(g0,g2)
    c: PointOnObject(g0,g-1)
    c: Coincident(g1,g2)
    c: PointOnObject(g1,g-3)
    c: Coincident(g4,g3)
    c: Distance(g4,g-3) = 0.1
    c: Distance(g-4,g3) = 3
FEATURE [PartDesign::Pad] Pad077
  Direction = (0,0,-1)
  Length = 10
  Length2 = 10
  Profile = -> Sketch120
  ReferenceAxis = -> Sketch120 [N_Axis]
  Refine = true
  Reversed = true
  SideType = 0
  Suppressed = false
  Type = 3
  Type2 = 0
  UpToFace = -> Binder033 [Face4]
FEATURE [Sketcher::SketchObject] Sketch125
  ArcFitTolerance = 1e-06
  AttachmentSupport = -> [Pad077]
  ExternalGeometry = -> [Binder033]
  ExternalTypes = [0,0,0]
  FullyConstrained = true
  MakeInternals = false
  MapMode = 5
  Placement = pos=(0,0,10) rot=(0,0,1;0rad)
  sketch-geometry (1):
    g0: Circle CenterX=0 CenterY=0 CenterZ=0 NormalX=0 NormalY=0 NormalZ=1 AngleXU=0 Radius=7.75
  constraints (2):
    c: Coincident(g0,g-3)
    c: Distance(g-5,g0) = 1.25
FEATURE [PartDesign::Pad] Pad080
  BaseFeature = -> Pad077
  Direction = (0,0,1)
  Length = 1.5
  Length2 = 10
  Profile = -> Sketch125
  ReferenceAxis = -> Sketch125 [N_Axis]
  Refine = true
  SideType = 0
  Suppressed = false
  Type = 0
  Type2 = 0
FEATURE [Sketcher::SketchObject] Sketch121
  ArcFitTolerance = 1e-06
  AttachmentSupport = -> [Pad080]
  ExternalGeometry = -> [Pad080]
  ExternalTypes = [0,0]
  FullyConstrained = false
  MakeInternals = false
  MapMode = 5
  Placement = pos=(0,0,11.5) rot=(0,0,1;0rad)
  sketch-geometry (7):
    g0: LineSegment StartX=-7.75 StartY=12.0494 StartZ=0 EndX=-9.75 EndY=12.0494 EndZ=0
    g1: LineSegment StartX=-9.75 StartY=12.0494 StartZ=0 EndX=-9.75 EndY=-12.0494 EndZ=0
    g2: LineSegment StartX=-9.75 StartY=-12.0494 StartZ=0 EndX=-7.75 EndY=-12.0494 EndZ=0
    g3: LineSegment StartX=-7.75 StartY=-12.0494 StartZ=0 EndX=-7.75 EndY=12.0494 EndZ=0
    g4: LineSegment [constr] StartX=-5.2 StartY=7.75 StartZ=0 EndX=-5.2 EndY=3.9 EndZ=0
    g5: GeomPoint [constr] X=-9.75 Y=0 Z=0
    g6: GeomPoint [constr] X=-7.75 Y=-3e-16 Z=0
  constraints (16):
    c: Coincident(g0,g1)
    c: Coincident(g1,g2)
    c: Coincident(g2,g3)
    c: Coincident(g3,g0)
    c: Horizontal(g0)
    c: Horizontal(g2)
    c: Vertical(g1)
    c: Vertical(g3)
    c: Vertical(g4)
    c: Symmetric(g1,g1,g5)
    c: Coincident(g4,g-4)
    c: Symmetric(g3,g3,g6)
    c: PointOnObject(g5,g-1)
    c: Distance(g0,g0) = 2
    c: PointOnObject(g6,g-5)
    c: PointOnObject(g0,g-6)
FEATURE [PartDesign::Pad] Pad078
  BaseFeature = -> Pad080
  Direction = (0,0,1)
  Length = 10
  Length2 = 10
  Offset = -4
  Profile = -> Sketch121
  ReferenceAxis = -> Sketch121 [N_Axis]
  Refine = true
  SideType = 0
  Suppressed = false
  Type = 3
  Type2 = 0
  UpToFace = -> Binder032 [Face11]
FEATURE [Sketcher::SketchObject] Sketch122
  ArcFitTolerance = 1e-06
  AttachmentSupport = -> [Pad078]
  ExternalGeometry = -> [Pad078]
  ExternalTypes = [0,0,0]
  FullyConstrained = true
  MakeInternals = false
  MapMode = 5
  Placement = pos=(-7.75,0,0) rot=(0.57735,0.57735,0.57735;2.0944rad)
  sketch-geometry (4):
    g0: LineSegment StartX=-12.0494 StartY=34.8 StartZ=0 EndX=-12.0494 EndY=32.8 EndZ=0
    g1: LineSegment StartX=-12.0494 StartY=32.8 StartZ=0 EndX=12.0494 EndY=32.8 EndZ=0
    g2: LineSegment StartX=12.0494 StartY=32.8 StartZ=0 EndX=12.0494 EndY=34.8 EndZ=0
    g3: LineSegment StartX=12.0494 StartY=34.8 StartZ=0 EndX=-12.0494 EndY=34.8 EndZ=0
  constraints (10):
    c: Coincident(g0,g1)
    c: Coincident(g1,g2)
    c: Coincident(g2,g3)
    c: Coincident(g3,g0)
    c: Vertical(g0)
    c: Vertical(g2)
    c: Horizontal(g1)
    c: DistanceY(g2,g2) = 2
    c: Coincident(g2,g-5)
    c: Coincident(g0,g-4)
FEATURE [PartDesign::Pad] Pad079
  BaseFeature = -> Pad078
  Direction = (1,0,0)
  Length = 10
  Length2 = 10
  Profile = -> Sketch122
  ReferenceAxis = -> Sketch122 [N_Axis]
  Refine = true
  SideType = 0
  Suppressed = false
  Type = 3
  Type2 = 0
  UpToFace = -> Binder032 [Face8]
FEATURE [PartDesign::Mirrored] Mirrored003
  BaseFeature = -> Pad079
  MirrorPlane = -> YZ_Plane028
  Originals = -> [Pad079,Pad077,Pad078]
  Refine = true
  Suppressed = false
  TransformMode = 0
FEATURE [PartDesign::Fillet] Fillet011
  Base = -> Mirrored003 [Edge35,Edge38,Edge41,Edge32]
  BaseFeature = -> Mirrored003
  Radius = 3
  Refine = true
  SupportTransform = false
  Suppressed = false
  UseAllEdges = false
FEATURE [Sketcher::SketchObject] Sketch123
  ArcFitTolerance = 1e-06
  AttachmentSupport = -> [Fillet011]
  ExternalGeometry = -> [Fillet011,Binder032]
  ExternalTypes = [0,0,0,0,0,0]
  FullyConstrained = true
  MakeInternals = false
  MapMode = 5
  Placement = pos=(9.75,-2.1e-15,2.1e-15) rot=(0.57735,0.57735,0.57735;2.0944rad)
  sketch-geometry (10):
    g0: LineSegment StartX=12.0494 StartY=11.5 StartZ=0 EndX=12.0494 EndY=14.8 EndZ=0
    g1: LineSegment StartX=12.0494 StartY=14.8 StartZ=0 EndX=2 EndY=14.8 EndZ=0
    g2: LineSegment StartX=2 StartY=14.8 StartZ=0 EndX=2 EndY=11.5 EndZ=0
    g3: LineSegment StartX=2 StartY=11.5 StartZ=0 EndX=12.0494 EndY=11.5 EndZ=0
    g4: LineSegment StartX=-12.0494 StartY=11.5 StartZ=0 EndX=-2 EndY=11.5 EndZ=0
    g5: LineSegment StartX=-2 StartY=11.5 StartZ=0 EndX=-2 EndY=14.8 EndZ=0
    g6: LineSegment StartX=-2 StartY=14.8 StartZ=0 EndX=-12.0494 EndY=14.8 EndZ=0
    g7: LineSegment StartX=-12.0494 StartY=14.8 StartZ=0 EndX=-12.0494 EndY=11.5 EndZ=0
    g8: LineSegment [constr] StartX=-2 StartY=14.8 StartZ=0 EndX=2 EndY=14.8 EndZ=0
    g9: GeomPoint [constr] X=1e-16 Y=14.8 Z=0
  constraints (25):
    c: Coincident(g0,g1)
    c: Coincident(g1,g2)
    c: Coincident(g2,g3)
    c: Coincident(g3,g0)
    c: Vertical(g0)
    c: Vertical(g2)
    c: Horizontal(g1)
    c: Horizontal(g3)
    c: Coincident(g0,g-5)
    c: Coincident(g4,g5)
    c: Coincident(g5,g6)
    c: Coincident(g6,g7)
    c: Coincident(g7,g4)
    c: Horizontal(g4)
    c: Horizontal(g6)
    c: Vertical(g5)
    c: Vertical(g7)
    c: Coincident(g4,g-5)
    c: PointOnObject(g-4,g6)
    c: PointOnObject(g-3,g1)
    c: Coincident(g8,g5)
    c: Coincident(g8,g1)
    c: Symmetric(g1,g5,g9)
    c: Equal(g6,g1)
    c: PointOnObject(g-6,g2)
FEATURE [PartDesign::Pocket] Pocket028
  BaseFeature = -> Fillet011
  Direction = (-1,0,0)
  Length = 5
  Length2 = 5
  Profile = -> Sketch123
  ReferenceAxis = -> Sketch123 [N_Axis]
  Refine = true
  SideType = 0
  Suppressed = false
  Type = 1
  Type2 = 0
FEATURE [PartDesign::Body] Body027  label="design5-coil-holder"
  AllowCompound = false
  Group = -> [Binder032,Binder033,Sketch120,Pad077,Sketch121,Sketch125,Pad080,Pad078,Sketch122,Pad079,Mirrored003,Fillet011,Sketch123,Pocket028]
  Origin = -> Origin061
  Tip = -> Pocket028
COMPONENT P20 — recipe-attached ("design6-mirror-attachment", modeled in this document).
Construction recipe (the document's own serialized feature program — sketch geometry with constraints, then the solid features built on it; lengths are millimeters unless a unit is written):

FEATURE [PartDesign::SubShapeBinder] Binder040
  BindCopyOnChange = 0
  BindMode = 0
  ClaimChildren = false
  Context = -> Body033 [Binder040.]
  Fuse = false
  MakeFace = true
  OffsetFill = false
  OffsetIntersection = false
  OffsetJoinType = 0
  OffsetOpenResult = false
  PartialLoad = false
  Refine = true
  Relative = true
  Support = -> [Body032]
  _Version = 2
FEATURE [Sketcher::SketchObject] Sketch157
  ArcFitTolerance = 1e-06
  AttachmentSupport = -> [Binder040]
  ExternalGeometry = -> [Binder040]
  ExternalTypes = [0,0,0,0,0]
  FullyConstrained = true
  MakeInternals = false
  MapMode = 5
  Placement = pos=(-2.28868e-11,-1.6904e-12,41.8) rot=(0,0,1;0rad)
  sketch-geometry (16):
    g0: LineSegment [constr] StartX=5.9 StartY=-4 StartZ=0 EndX=-5.9 EndY=4 EndZ=0
    g1: LineSegment [constr] StartX=5.9 StartY=-4 StartZ=0 EndX=5.9 EndY=-6 EndZ=0
    g2: LineSegment [constr] StartX=-5.9 StartY=4 StartZ=0 EndX=-5.9 EndY=6 EndZ=0
    g3: LineSegment StartX=1.9 StartY=-6 StartZ=0 EndX=5.9 EndY=-6 EndZ=0
    g4: LineSegment StartX=5.9 StartY=-6 StartZ=0 EndX=5.9 EndY=2 EndZ=0
    g5: LineSegment StartX=5.9 StartY=2 StartZ=0 EndX=1.9 EndY=2 EndZ=0
    g6: LineSegment [constr] StartX=1.9 StartY=0 StartZ=0 EndX=1.9 EndY=2 EndZ=0
    g7: LineSegment StartX=-5.9 StartY=6 StartZ=0 EndX=-5.9 EndY=4 EndZ=0
    g8: LineSegment StartX=-5.9 StartY=-2 StartZ=0 EndX=-5.9 EndY=4 EndZ=0
    g9: LineSegment StartX=1.9 StartY=2 StartZ=0 EndX=-1.9 EndY=2 EndZ=0
    g10: LineSegment StartX=-1.9 StartY=2 StartZ=0 EndX=-1.9 EndY=6 EndZ=0
    g11: LineSegment StartX=-1.9 StartY=6 StartZ=0 EndX=-5.9 EndY=6 EndZ=0
    g12: LineSegment [constr] StartX=-1.9 StartY=2 StartZ=0 EndX=-1.9 EndY=1.6829e-12 EndZ=0
    g13: LineSegment StartX=1.9 StartY=-6 StartZ=0 EndX=1.9 EndY=-2 EndZ=0
    g14: LineSegment StartX=1.9 StartY=-2 StartZ=0 EndX=-5.9 EndY=-2 EndZ=0
    g15: LineSegment [constr] StartX=-1.9 StartY=1.6829e-12 StartZ=0 EndX=-1.9 EndY=-2 EndZ=0
  constraints (42):
    c: Coincident(g0,g-3)
    c: Symmetric(g0,g0,g-1)
    c: Coincident(g1,g0)
    c: Vertical(g1)
    c: DistanceY(g1,g1) = 2
    c: Distance(g2) = 2
    c: Vertical(g2)
    c: Coincident(g0,g2)
    c: Coincident(g3,g1)
    c: Horizontal(g3)
    c: Coincident(g4,g1)
    c: Vertical(g4)
    c: Distance(g4,g-1) = 2
    c: Coincident(g5,g4)
    c: Horizontal(g5)
    c: Coincident(g6,g-5)
    c: Coincident(g6,g5)
    c: Vertical(g6)
    c: Coincident(g7,g2)
    c: Coincident(g7,g0)
    c: Coincident(g8,g0)
    c: Vertical(g8)
    c: Coincident(g9,g5)
    c: Horizontal(g9)
    c: Coincident(g10,g9)
    c: Vertical(g10)
    c: Coincident(g11,g10)
    c: Coincident(g11,g2)
    c: Horizontal(g11)
    c: Coincident(g12,g9)
    c: Coincident(g12,g-6)
    c: Vertical(g12)
    c: Coincident(g13,g3)
    c: Vertical(g13)
    c: Coincident(g14,g13)
    c: Horizontal(g14)
    c: Coincident(g8,g14)
    c: PointOnObject(g3,g-7)
    c: Vertical(g15)
    c: Equal(g15,g12)
    c: PointOnObject(g15,g14)
    c: Coincident(g15,g12)
FEATURE [PartDesign::Pad] Pad106
  Direction = (-5.475e-13,-4.04e-14,1)
  Length = 2
  Length2 = 10
  Profile = -> Sketch157
  ReferenceAxis = -> Sketch157 [N_Axis]
  Refine = true
  SideType = 0
  Suppressed = false
  Type = 0
  Type2 = 0
FEATURE [Sketcher::SketchObject] Sketch158
  ArcFitTolerance = 1e-06
  AttachmentSupport = -> [Pad106]
  ExternalGeometry = -> [Binder040,Pad106]
  ExternalTypes = [0,0,0,0,0,0,0,0,0,0]
  FullyConstrained = true
  MakeInternals = false
  MapMode = 5
  Placement = pos=(-2.2883e-11,-1.7034e-12,41.8) rot=(1,0,0;3.14159rad)
  sketch-geometry (17):
    g0: LineSegment StartX=1.9 StartY=4 StartZ=0 EndX=5.9 EndY=4 EndZ=0
    g1: LineSegment StartX=5.9 StartY=4 StartZ=0 EndX=5.9 EndY=6 EndZ=0
    g2: LineSegment StartX=5.9 StartY=6 StartZ=0 EndX=1.9 EndY=6 EndZ=0
    g3: LineSegment [constr] StartX=1.9 StartY=4 StartZ=0 EndX=-1.9 EndY=-4 EndZ=0
    g4: LineSegment StartX=-1.9 StartY=-4 StartZ=0 EndX=-5.9 EndY=-4 EndZ=0
    g5: LineSegment StartX=-5.9 StartY=-4 StartZ=0 EndX=-5.9 EndY=-6 EndZ=0
    g6: LineSegment StartX=-5.9 StartY=-6 StartZ=0 EndX=-1.9 EndY=-6 EndZ=0
    g7: LineSegment StartX=-1.9 StartY=-6 StartZ=0 EndX=-1.9 EndY=-4 EndZ=0
    g8: LineSegment StartX=1.9 StartY=6 StartZ=0 EndX=1.9 EndY=4 EndZ=0
    g9: LineSegment StartX=1.9 StartY=4.468e-13 StartZ=0 EndX=5.9 EndY=4.468e-13 EndZ=0
    g10: LineSegment StartX=5.9 StartY=2 StartZ=0 EndX=5.9 EndY=4.468e-13 EndZ=0
    g11: LineSegment StartX=-5.9 StartY=0 StartZ=0 EndX=-1.9 EndY=0 EndZ=0
    g12: LineSegment [constr] StartX=-1.9 StartY=-2 StartZ=0 EndX=-1.9 EndY=0 EndZ=0
    g13: LineSegment StartX=-5.9 StartY=0 StartZ=0 EndX=-5.9 EndY=-2 EndZ=0
    g14: LineSegment StartX=-5.9 StartY=-2 StartZ=0 EndX=-3.4 EndY=-2 EndZ=0
    g15: ArcOfCircle CenterX=-3.4 CenterY=-0.5 CenterZ=0 NormalX=0 NormalY=0 NormalZ=1 AngleXU=0 Radius=1.5 StartAngle=4.71239 EndAngle=6.28318
    g16: LineSegment StartX=-1.9 StartY=-0.5 StartZ=0 EndX=-1.9 EndY=0 EndZ=0
  constraints (44):
    c: Coincident(g0,g1)
    c: Coincident(g1,g2)
    c: Horizontal(g2)
    c: Coincident(g0,g-3)
    c: Coincident(g3,g0)
    c: Symmetric(g3,g0,g-1)
    c: Coincident(g4,g5)
    c: Coincident(g5,g6)
    c: Coincident(g6,g7)
    c: Coincident(g7,g4)
    c: Horizontal(g4)
    c: Horizontal(g6)
    c: Vertical(g5)
    c: Vertical(g7)
    c: Coincident(g4,g3)
    c: Coincident(g5,g-7)
    c: Coincident(g0,g-8)
    c: Coincident(g1,g-4)
    c: PointOnObject(g2,g-8)
    c: Coincident(g8,g2)
    c: Coincident(g8,g0)
    c: Coincident(g9,g-11)
    c: PointOnObject(g9,g-4)
    c: Horizontal(g9)
    c: Coincident(g10,g-10)
    c: Coincident(g10,g9)
    c: PointOnObject(g11,g-5)
    c: PointOnObject(g11,g-1)
    c: Horizontal(g11)
    c: Coincident(g12,g-6)
    c: Vertical(g12)
    c: Coincident(g11,g12)
    c: PointOnObject(g13,g-5)
    c: Coincident(g14,g13)
    c: Horizontal(g14)
    c: Angle(g15) = 1.5708
    c: Coincident(g15,g14)
    c: Coincident(g16,g15)
    c: Coincident(g16,g11)
    c: Vertical(g16)
    c: Equal(g-11,g16)
    c: Equal(g14,g-10)
    c: Equal(g15,g-9)
    c: Coincident(g13,g11)
FEATURE [PartDesign::Pad] Pad107
  BaseFeature = -> Pad106
  Direction = (5.474e-13,4.08e-14,-1)
  Length = 10
  Length2 = 10
  Profile = -> Sketch158
  ReferenceAxis = -> Sketch158 [N_Axis]
  Refine = true
  SideType = 0
  Suppressed = false
  Type = 3
  Type2 = 0
  UpToFace = -> Binder040 [Face16]
FEATURE [PartDesign::Body] Body033  label="design6-mirror-attachment"
  AllowCompound = false
  Group = -> [Binder040,Sketch157,Pad106,Sketch158,Pad107]
  Origin = -> Origin073
  Tip = -> Pad107
